# Revit family: 879-006X99-001-DN65-600
name_source: partatom
category: Pipe Accessories
units: mm (PartAtom-declared; Revit-internal decimal feet)

## family parameters
Always vertical = Yes
Cut with Voids When Loaded = No
Part Type = Valve - Breaks Into
Round Connector Dimension = Use Diameter
Shared = No
Work Plane-Based = No

## types (49) — shared parameters
879-0065-00-14400609999 = DN65_PN10/16
879-0065-00-14400619999 = DN65_PN10/16
879-0065-00-14400629999 = DN65_PN10/16
879-0065-00-144006299A0 = DN65_PN10/16
879-0080-00-14400609999 = DN80_PN10/16
879-0080-00-14400619999 = DN80_PN10/16
879-0080-00-14400629999 = DN80_PN10/16
879-0080-00-144006299A0 = DN80_PN10/16
879-0100-00-14400609999 = DN100_PN10/16
879-0100-00-14400619999 = DN100_PN10/16
879-0100-00-14400629999 = DN100_PN10/16
879-0100-00-144006299A0 = DN100_PN10/16
879-0125-00-14400609999 = DN125_PN10/16
879-0125-00-14400619999 = DN125_PN10/16
879-0125-00-14400629999 = DN125_PN10/16
879-0125-00-144006299A0 = DN125_PN10/16
879-0150-00-14400609999 = DN150_PN10/16
879-0150-00-14400619999 = DN150_PN10/16
879-0150-00-14400629999 = DN150_PN10/16
879-0150-00-144006299A0 = DN150_PN10/16
879-0200-00-04400609999 = DN200_PN10
879-0200-00-04400619999 = DN200_PN10
879-0200-00-04400629999 = DN200_PN10
879-0200-00-14400609999 = DN200_PN16
879-0200-00-14400619999 = DN200_PN16
879-0200-00-14400629999 = DN200_PN16
879-0200-00-144006299A0 = DN200_PN16
879-0250-00-04400609999 = DN250_PN10
879-0250-00-04400619999 = DN250_PN10
879-0250-00-04400629999 = DN250_PN10
879-0250-00-14400609999 = DN250_PN16
879-0250-00-14400619999 = DN250_PN16
879-0250-00-14400629999 = DN250_PN16
879-0250-00-144006299A0 = DN250_PN16
879-0300-00-04400609999 = DN300_PN10
879-0300-00-04400619999 = DN300_PN10
879-0300-00-04400629999 = DN300_PN10
879-0300-00-14400609999 = DN300_PN16
879-0300-00-14400619999 = DN300_PN16
879-0300-00-14400629999 = DN300_PN16
879-0300-00-144006299A0 = DN300_PN16
879-0350-00-04400609999 = DN350_PN10
879-0350-00-04400619999 = DN350_PN10
879-0350-00-04400629999 = DN350_PN10
879-0350-00-144006299A0 = DN350_PN16
879-0400-00-144006299A0 = DN400_PN16
879-0450-00-144006299A0 = DN450_PN16
879-0500-00-144006299A0 = DN500_PN16
879-0600-00-144006299A0 = DN600_PN16
Body_wall_thickness = 10 mm  [stored 0.0328084 ft]
Description_ = AVK ON/OFF FLOAT LEVEL CONTROL VALVE
Search_Table = 879-006X99-001-DN65-600
URL product pages = https://www.avkvalves.com

## per-type parameters (varying)
- 879-0065-00-14400609999_DN65_PN10/16: Body_Collar_Dia=30 mm  [stored 0.0984252 ft]; Body_Collar_Dia_2=21 mm  [stored 0.0688976 ft]; Body_Flange_Dia=94 mm; Body_Flange_Dia_2=104 mm; Body_Height_1=64 mm; Body_Height_2=36 mm  [stored 0.11811 ft]; Body_Height_3=45 mm; Body_Height_4=51 mm; Body_Top_Dia=13 mm; Body_Top_Dia_2=11 mm; Body_With_Dia=36 mm  [stored 0.11811 ft]; Body_With_Dia_1=73 mm; Body_With_Dia_2=78 mm; Bolt_support=223 mm; Bolt_support_2=112 mm; Bolt_support_Dia=12 mm  [stored 0.0393701 ft]; Bolt_support_lenght=53 mm; Bolt_support_lenght_2=63 mm; Bottom_profile=16 mm  [stored 0.0524934 ft]; D1=59 mm; D3=93 mm; DN=65 mm; Fillet_Length=6 mm  [stored 0.019685 ft]; Fillet_Length_Ref=18 mm  [stored 0.0590551 ft]; Flange_thickness=19 mm  [stored 0.062336 ft]; H=290 mm; H3_Ref=284 mm; ID=33 mm; L=290 mm; PG_Dia=33 mm; PG_Ref=43 mm  [stored 0.141076 ft]; PG_depth=8 mm  [stored 0.0262467 ft]; PG_height=198 mm; PG_height_1=182 mm; PG_ref=43 mm  [stored 0.141076 ft]; P_lenght=39 mm  [stored 0.127953 ft]; Pilot_Dia_1=18 mm  [stored 0.0590551 ft]; Pilot_Dia_2=35 mm  [stored 0.114829 ft]; Pilot_Dia_3=12 mm  [stored 0.0393701 ft]; Pilot_Dia_4=6 mm  [stored 0.019685 ft]; Pilot_Dia_5=4 mm  [stored 0.0131234 ft]; Pilot_top_1=187 mm; Profile1_Height=117 mm; Profile1_Length=25 mm  [stored 0.082021 ft]; Profile1_Length_2=17 mm; Profile_Dia=6 mm  [stored 0.019685 ft]; Profile_Dia_2=6 mm  [stored 0.019685 ft]; Profile_Dia_3=12 mm  [stored 0.0393701 ft]; Profile_height ref=41 mm  [stored 0.134514 ft]; Top_Profile=134 mm; Top_Profile_Ref=139 mm; W=259 mm; W_Ref=253 mm
- 879-0065-00-14400619999_DN65_PN10/16: Body_Collar_Dia=30 mm  [stored 0.0984252 ft]; Body_Collar_Dia_2=21 mm  [stored 0.0688976 ft]; Body_Flange_Dia=94 mm; Body_Flange_Dia_2=104 mm; Body_Height_1=64 mm; Body_Height_2=36 mm  [stored 0.11811 ft]; Body_Height_3=45 mm; Body_Height_4=51 mm; Body_Top_Dia=13 mm; Body_Top_Dia_2=11 mm; Body_With_Dia=36 mm  [stored 0.11811 ft]; Body_With_Dia_1=73 mm; Body_With_Dia_2=78 mm; Bolt_support=223 mm; Bolt_support_2=112 mm; Bolt_support_Dia=12 mm  [stored 0.0393701 ft]; Bolt_support_lenght=53 mm; Bolt_support_lenght_2=63 mm; Bottom_profile=16 mm  [stored 0.0524934 ft]; D1=59 mm; D3=93 mm; DN=65 mm; Fillet_Length=6 mm  [stored 0.019685 ft]; Fillet_Length_Ref=18 mm  [stored 0.0590551 ft]; Flange_thickness=19 mm  [stored 0.062336 ft]; H=290 mm; H3_Ref=284 mm; ID=33 mm; L=290 mm; PG_Dia=33 mm; PG_Ref=43 mm  [stored 0.141076 ft]; PG_depth=8 mm  [stored 0.0262467 ft]; PG_height=212 mm; PG_height_1=196 mm; PG_ref=43 mm  [stored 0.141076 ft]; P_lenght=39 mm  [stored 0.127953 ft]; Pilot_Dia_1=18 mm  [stored 0.0590551 ft]; Pilot_Dia_2=35 mm  [stored 0.114829 ft]; Pilot_Dia_3=12 mm  [stored 0.0393701 ft]; Pilot_Dia_4=6 mm  [stored 0.019685 ft]; Pilot_Dia_5=4 mm  [stored 0.0131234 ft]; Pilot_top_1=187 mm; Profile1_Height=135 mm; Profile1_Length=25 mm  [stored 0.082021 ft]; Profile1_Length_2=17 mm; Profile_Dia=6 mm  [stored 0.019685 ft]; Profile_Dia_2=6 mm  [stored 0.019685 ft]; Profile_Dia_3=12 mm  [stored 0.0393701 ft]; Profile_height ref=41 mm  [stored 0.134514 ft]; Top_Profile=134 mm; Top_Profile_Ref=139 mm; W=259 mm; W_Ref=253 mm
- 879-0065-00-14400629999_DN65_PN10/16: Body_Collar_Dia=30 mm  [stored 0.0984252 ft]; Body_Collar_Dia_2=21 mm  [stored 0.0688976 ft]; Body_Flange_Dia=94 mm; Body_Flange_Dia_2=104 mm; Body_Height_1=64 mm; Body_Height_2=36 mm  [stored 0.11811 ft]; Body_Height_3=45 mm; Body_Height_4=51 mm; Body_Top_Dia=13 mm; Body_Top_Dia_2=11 mm; Body_With_Dia=36 mm  [stored 0.11811 ft]; Body_With_Dia_1=73 mm; Body_With_Dia_2=78 mm; Bolt_support=223 mm; Bolt_support_2=112 mm; Bolt_support_Dia=12 mm  [stored 0.0393701 ft]; Bolt_support_lenght=53 mm; Bolt_support_lenght_2=63 mm; Bottom_profile=16 mm  [stored 0.0524934 ft]; D1=59 mm; D3=93 mm; DN=65 mm; Fillet_Length=6 mm  [stored 0.019685 ft]; Fillet_Length_Ref=18 mm  [stored 0.0590551 ft]; Flange_thickness=19 mm  [stored 0.062336 ft]; H=290 mm; H3_Ref=284 mm; ID=33 mm; L=290 mm; PG_Dia=33 mm; PG_Ref=43 mm  [stored 0.141076 ft]; PG_depth=8 mm  [stored 0.0262467 ft]; PG_height=198 mm; PG_height_1=182 mm; PG_ref=43 mm  [stored 0.141076 ft]; P_lenght=39 mm  [stored 0.127953 ft]; Pilot_Dia_1=18 mm  [stored 0.0590551 ft]; Pilot_Dia_2=35 mm  [stored 0.114829 ft]; Pilot_Dia_3=12 mm  [stored 0.0393701 ft]; Pilot_Dia_4=6 mm  [stored 0.019685 ft]; Pilot_Dia_5=4 mm  [stored 0.0131234 ft]; Pilot_top_1=187 mm; Profile1_Height=117 mm; Profile1_Length=25 mm  [stored 0.082021 ft]; Profile1_Length_2=17 mm; Profile_Dia=6 mm  [stored 0.019685 ft]; Profile_Dia_2=6 mm  [stored 0.019685 ft]; Profile_Dia_3=12 mm  [stored 0.0393701 ft]; Profile_height ref=41 mm  [stored 0.134514 ft]; Top_Profile=134 mm; Top_Profile_Ref=139 mm; W=259 mm; W_Ref=253 mm
- 879-0065-00-144006299A0_DN65_PN10/16: Body_Collar_Dia=30 mm  [stored 0.0984252 ft]; Body_Collar_Dia_2=21 mm  [stored 0.0688976 ft]; Body_Flange_Dia=94 mm; Body_Flange_Dia_2=104 mm; Body_Height_1=64 mm; Body_Height_2=36 mm  [stored 0.11811 ft]; Body_Height_3=73 mm; Body_Height_4=51 mm; Body_Top_Dia=13 mm; Body_Top_Dia_2=11 mm; Body_With_Dia=36 mm  [stored 0.11811 ft]; Body_With_Dia_1=73 mm; Body_With_Dia_2=78 mm; Bolt_support=223 mm; Bolt_support_2=112 mm; Bolt_support_Dia=12 mm  [stored 0.0393701 ft]; Bolt_support_lenght=53 mm; Bolt_support_lenght_2=63 mm; Bottom_profile=16 mm  [stored 0.0524934 ft]; D1=59 mm; D3=93 mm; DN=65 mm; Fillet_Length=6 mm  [stored 0.019685 ft]; Fillet_Length_Ref=18 mm  [stored 0.0590551 ft]; Flange_thickness=19 mm  [stored 0.062336 ft]; H=424 mm; H3_Ref=418 mm; ID=33 mm; L=290 mm; PG_Dia=33 mm; PG_Ref=43 mm  [stored 0.141076 ft]; PG_depth=8 mm  [stored 0.0262467 ft]; PG_height=242 mm; PG_height_1=226 mm; PG_ref=43 mm  [stored 0.141076 ft]; P_lenght=39 mm  [stored 0.127953 ft]; Pilot_Dia_1=18 mm  [stored 0.0590551 ft]; Pilot_Dia_2=35 mm  [stored 0.114829 ft]; Pilot_Dia_3=12 mm  [stored 0.0393701 ft]; Pilot_Dia_4=6 mm  [stored 0.019685 ft]; Pilot_Dia_5=4 mm  [stored 0.0131234 ft]; Pilot_top_1=261 mm; Profile1_Height=135 mm; Profile1_Length=25 mm  [stored 0.082021 ft]; Profile1_Length_2=17 mm; Profile_Dia=6 mm  [stored 0.019685 ft]; Profile_Dia_2=6 mm  [stored 0.019685 ft]; Profile_Dia_3=12 mm  [stored 0.0393701 ft]; Profile_height ref=41 mm  [stored 0.134514 ft]; Top_Profile=134 mm; Top_Profile_Ref=139 mm; W=259 mm; W_Ref=253 mm
- 879-0080-00-14400609999_DN80_PN10/16: Body_Collar_Dia=32 mm; Body_Collar_Dia_2=22 mm  [stored 0.0721785 ft]; Body_Flange_Dia=100 mm; Body_Flange_Dia_2=111 mm; Body_Height_1=69 mm; Body_Height_2=39 mm  [stored 0.127953 ft]; Body_Height_3=50 mm; Body_Height_4=54 mm; Body_Top_Dia=14 mm  [stored 0.0459318 ft]; Body_Top_Dia_2=12 mm  [stored 0.0393701 ft]; Body_With_Dia=39 mm  [stored 0.127953 ft]; Body_With_Dia_1=78 mm; Body_With_Dia_2=84 mm; Bolt_support=238 mm; Bolt_support_2=119 mm; Bolt_support_Dia=12 mm  [stored 0.0393701 ft]; Bolt_support_lenght=60 mm; Bolt_support_lenght_2=70 mm; Bottom_profile=20 mm  [stored 0.0656168 ft]; D1=66 mm; D3=100 mm; DN=80 mm; Fillet_Length=6 mm  [stored 0.019685 ft]; Fillet_Length_Ref=18 mm  [stored 0.0590551 ft]; Flange_thickness=19 mm  [stored 0.062336 ft]; H=307 mm; H3_Ref=301 mm; ID=40 mm  [stored 0.131234 ft]; L=310 mm; PG_Dia=40 mm  [stored 0.131234 ft]; PG_Ref=46 mm; PG_depth=8 mm  [stored 0.0262467 ft]; PG_height=229 mm; PG_height_1=209 mm; PG_ref=50 mm; P_lenght=43 mm  [stored 0.141076 ft]; Pilot_Dia_1=20 mm  [stored 0.0656168 ft]; Pilot_Dia_2=39 mm  [stored 0.127953 ft]; Pilot_Dia_3=13 mm; Pilot_Dia_4=7 mm  [stored 0.0229659 ft]; Pilot_Dia_5=4 mm  [stored 0.0131234 ft]; Pilot_top_1=197 mm; Profile1_Height=144 mm; Profile1_Length=27 mm; Profile1_Length_2=18 mm  [stored 0.0590551 ft]; Profile_Dia=6 mm  [stored 0.019685 ft]; Profile_Dia_2=6 mm  [stored 0.019685 ft]; Profile_Dia_3=12 mm  [stored 0.0393701 ft]; Profile_height ref=41 mm  [stored 0.134514 ft]; Top_Profile=143 mm; Top_Profile_Ref=148 mm; W=281 mm; W_Ref=275 mm
- 879-0080-00-14400619999_DN80_PN10/16: Body_Collar_Dia=32 mm; Body_Collar_Dia_2=22 mm  [stored 0.0721785 ft]; Body_Flange_Dia=100 mm; Body_Flange_Dia_2=111 mm; Body_Height_1=69 mm; Body_Height_2=39 mm  [stored 0.127953 ft]; Body_Height_3=50 mm; Body_Height_4=54 mm; Body_Top_Dia=14 mm  [stored 0.0459318 ft]; Body_Top_Dia_2=12 mm  [stored 0.0393701 ft]; Body_With_Dia=39 mm  [stored 0.127953 ft]; Body_With_Dia_1=78 mm; Body_With_Dia_2=84 mm; Bolt_support=238 mm; Bolt_support_2=119 mm; Bolt_support_Dia=12 mm  [stored 0.0393701 ft]; Bolt_support_lenght=60 mm; Bolt_support_lenght_2=70 mm; Bottom_profile=20 mm  [stored 0.0656168 ft]; D1=66 mm; D3=100 mm; DN=80 mm; Fillet_Length=6 mm  [stored 0.019685 ft]; Fillet_Length_Ref=18 mm  [stored 0.0590551 ft]; Flange_thickness=19 mm  [stored 0.062336 ft]; H=307 mm; H3_Ref=301 mm; ID=40 mm  [stored 0.131234 ft]; L=310 mm; PG_Dia=40 mm  [stored 0.131234 ft]; PG_Ref=46 mm; PG_depth=8 mm  [stored 0.0262467 ft]; PG_height=220 mm; PG_height_1=200 mm; PG_ref=50 mm; P_lenght=43 mm  [stored 0.141076 ft]; Pilot_Dia_1=20 mm  [stored 0.0656168 ft]; Pilot_Dia_2=39 mm  [stored 0.127953 ft]; Pilot_Dia_3=13 mm; Pilot_Dia_4=7 mm  [stored 0.0229659 ft]; Pilot_Dia_5=4 mm  [stored 0.0131234 ft]; Pilot_top_1=197 mm; Profile1_Height=133 mm; Profile1_Length=27 mm; Profile1_Length_2=18 mm  [stored 0.0590551 ft]; Profile_Dia=6 mm  [stored 0.019685 ft]; Profile_Dia_2=6 mm  [stored 0.019685 ft]; Profile_Dia_3=12 mm  [stored 0.0393701 ft]; Profile_height ref=41 mm  [stored 0.134514 ft]; Top_Profile=143 mm; Top_Profile_Ref=148 mm; W=281 mm; W_Ref=275 mm
- 879-0080-00-14400629999_DN80_PN10/16: Body_Collar_Dia=32 mm; Body_Collar_Dia_2=22 mm  [stored 0.0721785 ft]; Body_Flange_Dia=100 mm; Body_Flange_Dia_2=111 mm; Body_Height_1=69 mm; Body_Height_2=39 mm  [stored 0.127953 ft]; Body_Height_3=50 mm; Body_Height_4=54 mm; Body_Top_Dia=14 mm  [stored 0.0459318 ft]; Body_Top_Dia_2=12 mm  [stored 0.0393701 ft]; Body_With_Dia=39 mm  [stored 0.127953 ft]; Body_With_Dia_1=78 mm; Body_With_Dia_2=84 mm; Bolt_support=238 mm; Bolt_support_2=119 mm; Bolt_support_Dia=12 mm  [stored 0.0393701 ft]; Bolt_support_lenght=60 mm; Bolt_support_lenght_2=70 mm; Bottom_profile=20 mm  [stored 0.0656168 ft]; D1=66 mm; D3=100 mm; DN=80 mm; Fillet_Length=6 mm  [stored 0.019685 ft]; Fillet_Length_Ref=18 mm  [stored 0.0590551 ft]; Flange_thickness=19 mm  [stored 0.062336 ft]; H=307 mm; H3_Ref=301 mm; ID=40 mm  [stored 0.131234 ft]; L=310 mm; PG_Dia=40 mm  [stored 0.131234 ft]; PG_Ref=46 mm; PG_depth=8 mm  [stored 0.0262467 ft]; PG_height=229 mm; PG_height_1=209 mm; PG_ref=50 mm; P_lenght=43 mm  [stored 0.141076 ft]; Pilot_Dia_1=20 mm  [stored 0.0656168 ft]; Pilot_Dia_2=39 mm  [stored 0.127953 ft]; Pilot_Dia_3=13 mm; Pilot_Dia_4=7 mm  [stored 0.0229659 ft]; Pilot_Dia_5=4 mm  [stored 0.0131234 ft]; Pilot_top_1=197 mm; Profile1_Height=144 mm; Profile1_Length=27 mm; Profile1_Length_2=18 mm  [stored 0.0590551 ft]; Profile_Dia=6 mm  [stored 0.019685 ft]; Profile_Dia_2=6 mm  [stored 0.019685 ft]; Profile_Dia_3=12 mm  [stored 0.0393701 ft]; Profile_height ref=41 mm  [stored 0.134514 ft]; Top_Profile=143 mm; Top_Profile_Ref=148 mm; W=281 mm; W_Ref=275 mm
- 879-0080-00-144006299A0_DN80_PN10/16: Body_Collar_Dia=32 mm; Body_Collar_Dia_2=22 mm  [stored 0.0721785 ft]; Body_Flange_Dia=100 mm; Body_Flange_Dia_2=111 mm; Body_Height_1=69 mm; Body_Height_2=39 mm  [stored 0.127953 ft]; Body_Height_3=78 mm; Body_Height_4=54 mm; Body_Top_Dia=14 mm  [stored 0.0459318 ft]; Body_Top_Dia_2=12 mm  [stored 0.0393701 ft]; Body_With_Dia=39 mm  [stored 0.127953 ft]; Body_With_Dia_1=78 mm; Body_With_Dia_2=84 mm; Bolt_support=238 mm; Bolt_support_2=119 mm; Bolt_support_Dia=12 mm  [stored 0.0393701 ft]; Bolt_support_lenght=60 mm; Bolt_support_lenght_2=70 mm; Bottom_profile=20 mm  [stored 0.0656168 ft]; D1=66 mm; D3=100 mm; DN=80 mm; Fillet_Length=6 mm  [stored 0.019685 ft]; Fillet_Length_Ref=18 mm  [stored 0.0590551 ft]; Flange_thickness=19 mm  [stored 0.062336 ft]; H=447 mm; H3_Ref=441 mm; ID=40 mm  [stored 0.131234 ft]; L=310 mm; PG_Dia=40 mm  [stored 0.131234 ft]; PG_Ref=46 mm; PG_depth=8 mm  [stored 0.0262467 ft]; PG_height=252 mm; PG_height_1=232 mm; PG_ref=50 mm; P_lenght=43 mm  [stored 0.141076 ft]; Pilot_Dia_1=20 mm  [stored 0.0656168 ft]; Pilot_Dia_2=39 mm  [stored 0.127953 ft]; Pilot_Dia_3=13 mm; Pilot_Dia_4=7 mm  [stored 0.0229659 ft]; Pilot_Dia_5=4 mm  [stored 0.0131234 ft]; Pilot_top_1=275 mm; Profile1_Height=133 mm; Profile1_Length=27 mm; Profile1_Length_2=18 mm  [stored 0.0590551 ft]; Profile_Dia=6 mm  [stored 0.019685 ft]; Profile_Dia_2=6 mm  [stored 0.019685 ft]; Profile_Dia_3=12 mm  [stored 0.0393701 ft]; Profile_height ref=41 mm  [stored 0.134514 ft]; Top_Profile=143 mm; Top_Profile_Ref=148 mm; W=281 mm; W_Ref=275 mm
- 879-0100-00-14400609999_DN100_PN10/16: Body_Collar_Dia=36 mm  [stored 0.11811 ft]; Body_Collar_Dia_2=25 mm  [stored 0.082021 ft]; Body_Flange_Dia=113 mm; Body_Flange_Dia_2=125 mm; Body_Height_1=78 mm; Body_Height_2=44 mm; Body_Height_3=40 mm  [stored 0.131234 ft]; Body_Height_4=59 mm; Body_Top_Dia=16 mm  [stored 0.0524934 ft]; Body_Top_Dia_2=13 mm; Body_With_Dia=44 mm; Body_With_Dia_1=88 mm; Body_With_Dia_2=95 mm; Bolt_support=269 mm; Bolt_support_2=135 mm; Bolt_support_Dia=12 mm  [stored 0.0393701 ft]; Bolt_support_lenght=70 mm; Bolt_support_lenght_2=80 mm; Bottom_profile=25 mm  [stored 0.082021 ft]; D1=78 mm; D3=110 mm; DN=100 mm; Fillet_Length=6 mm  [stored 0.019685 ft]; Fillet_Length_Ref=18 mm  [stored 0.0590551 ft]; Flange_thickness=19 mm  [stored 0.062336 ft]; H=322 mm; H3_Ref=316 mm; ID=50 mm; L=350 mm; PG_Dia=50 mm; PG_Ref=52 mm; PG_depth=8 mm  [stored 0.0262467 ft]; PG_height=244 mm; PG_height_1=219 mm; PG_ref=60 mm; P_lenght=48 mm; Pilot_Dia_1=22 mm  [stored 0.0721785 ft]; Pilot_Dia_2=44 mm; Pilot_Dia_3=15 mm  [stored 0.0492126 ft]; Pilot_Dia_4=7 mm  [stored 0.0229659 ft]; Pilot_Dia_5=5 mm  [stored 0.0164042 ft]; Pilot_top_1=205 mm; Profile1_Height=150 mm; Profile1_Length=30 mm  [stored 0.0984252 ft]; Profile1_Length_2=20 mm  [stored 0.0656168 ft]; Profile_Dia=6 mm  [stored 0.019685 ft]; Profile_Dia_2=6 mm  [stored 0.019685 ft]; Profile_Dia_3=12 mm  [stored 0.0393701 ft]; Profile_height ref=41 mm  [stored 0.134514 ft]; Top_Profile=162 mm; Top_Profile_Ref=167 mm; W=300 mm; W_Ref=294 mm
- 879-0100-00-14400619999_DN100_PN10/16: Body_Collar_Dia=36 mm  [stored 0.11811 ft]; Body_Collar_Dia_2=25 mm  [stored 0.082021 ft]; Body_Flange_Dia=113 mm; Body_Flange_Dia_2=125 mm; Body_Height_1=78 mm; Body_Height_2=44 mm; Body_Height_3=40 mm  [stored 0.131234 ft]; Body_Height_4=59 mm; Body_Top_Dia=16 mm  [stored 0.0524934 ft]; Body_Top_Dia_2=13 mm; Body_With_Dia=44 mm; Body_With_Dia_1=88 mm; Body_With_Dia_2=95 mm; Bolt_support=269 mm; Bolt_support_2=135 mm; Bolt_support_Dia=12 mm  [stored 0.0393701 ft]; Bolt_support_lenght=70 mm; Bolt_support_lenght_2=80 mm; Bottom_profile=25 mm  [stored 0.082021 ft]; D1=78 mm; D3=110 mm; DN=100 mm; Fillet_Length=6 mm  [stored 0.019685 ft]; Fillet_Length_Ref=18 mm  [stored 0.0590551 ft]; Flange_thickness=19 mm  [stored 0.062336 ft]; H=322 mm; H3_Ref=316 mm; ID=50 mm; L=350 mm; PG_Dia=50 mm; PG_Ref=52 mm; PG_depth=8 mm  [stored 0.0262467 ft]; PG_height=237 mm; PG_height_1=212 mm; PG_ref=60 mm; P_lenght=48 mm; Pilot_Dia_1=22 mm  [stored 0.0721785 ft]; Pilot_Dia_2=44 mm; Pilot_Dia_3=15 mm  [stored 0.0492126 ft]; Pilot_Dia_4=7 mm  [stored 0.0229659 ft]; Pilot_Dia_5=5 mm  [stored 0.0164042 ft]; Pilot_top_1=205 mm; Profile1_Height=141 mm; Profile1_Length=30 mm  [stored 0.0984252 ft]; Profile1_Length_2=20 mm  [stored 0.0656168 ft]; Profile_Dia=6 mm  [stored 0.019685 ft]; Profile_Dia_2=6 mm  [stored 0.019685 ft]; Profile_Dia_3=12 mm  [stored 0.0393701 ft]; Profile_height ref=41 mm  [stored 0.134514 ft]; Top_Profile=162 mm; Top_Profile_Ref=167 mm; W=300 mm; W_Ref=294 mm
- 879-0100-00-14400629999_DN100_PN10/16: Body_Collar_Dia=36 mm  [stored 0.11811 ft]; Body_Collar_Dia_2=25 mm  [stored 0.082021 ft]; Body_Flange_Dia=113 mm; Body_Flange_Dia_2=125 mm; Body_Height_1=78 mm; Body_Height_2=44 mm; Body_Height_3=40 mm  [stored 0.131234 ft]; Body_Height_4=59 mm; Body_Top_Dia=16 mm  [stored 0.0524934 ft]; Body_Top_Dia_2=13 mm; Body_With_Dia=44 mm; Body_With_Dia_1=88 mm; Body_With_Dia_2=95 mm; Bolt_support=269 mm; Bolt_support_2=135 mm; Bolt_support_Dia=12 mm  [stored 0.0393701 ft]; Bolt_support_lenght=70 mm; Bolt_support_lenght_2=80 mm; Bottom_profile=25 mm  [stored 0.082021 ft]; D1=78 mm; D3=110 mm; DN=100 mm; Fillet_Length=6 mm  [stored 0.019685 ft]; Fillet_Length_Ref=18 mm  [stored 0.0590551 ft]; Flange_thickness=19 mm  [stored 0.062336 ft]; H=322 mm; H3_Ref=316 mm; ID=50 mm; L=350 mm; PG_Dia=50 mm; PG_Ref=52 mm; PG_depth=8 mm  [stored 0.0262467 ft]; PG_height=244 mm; PG_height_1=219 mm; PG_ref=60 mm; P_lenght=48 mm; Pilot_Dia_1=22 mm  [stored 0.0721785 ft]; Pilot_Dia_2=44 mm; Pilot_Dia_3=15 mm  [stored 0.0492126 ft]; Pilot_Dia_4=7 mm  [stored 0.0229659 ft]; Pilot_Dia_5=5 mm  [stored 0.0164042 ft]; Pilot_top_1=205 mm; Profile1_Height=150 mm; Profile1_Length=30 mm  [stored 0.0984252 ft]; Profile1_Length_2=20 mm  [stored 0.0656168 ft]; Profile_Dia=6 mm  [stored 0.019685 ft]; Profile_Dia_2=6 mm  [stored 0.019685 ft]; Profile_Dia_3=12 mm  [stored 0.0393701 ft]; Profile_height ref=41 mm  [stored 0.134514 ft]; Top_Profile=162 mm; Top_Profile_Ref=167 mm; W=300 mm; W_Ref=294 mm
- 879-0100-00-144006299A0_DN100_PN10/16: Body_Collar_Dia=36 mm  [stored 0.11811 ft]; Body_Collar_Dia_2=25 mm  [stored 0.082021 ft]; Body_Flange_Dia=113 mm; Body_Flange_Dia_2=125 mm; Body_Height_1=78 mm; Body_Height_2=44 mm; Body_Height_3=70 mm; Body_Height_4=59 mm; Body_Top_Dia=16 mm  [stored 0.0524934 ft]; Body_Top_Dia_2=13 mm; Body_With_Dia=44 mm; Body_With_Dia_1=88 mm; Body_With_Dia_2=95 mm; Bolt_support=269 mm; Bolt_support_2=135 mm; Bolt_support_Dia=12 mm  [stored 0.0393701 ft]; Bolt_support_lenght=70 mm; Bolt_support_lenght_2=80 mm; Bottom_profile=25 mm  [stored 0.082021 ft]; D1=78 mm; D3=110 mm; DN=100 mm; Fillet_Length=6 mm  [stored 0.019685 ft]; Fillet_Length_Ref=18 mm  [stored 0.0590551 ft]; Flange_thickness=19 mm  [stored 0.062336 ft]; H=461 mm; H3_Ref=455 mm; ID=50 mm; L=350 mm; PG_Dia=50 mm; PG_Ref=52 mm; PG_depth=8 mm  [stored 0.0262467 ft]; PG_height=269 mm; PG_height_1=244 mm; PG_ref=60 mm; P_lenght=48 mm; Pilot_Dia_1=22 mm  [stored 0.0721785 ft]; Pilot_Dia_2=44 mm; Pilot_Dia_3=15 mm  [stored 0.0492126 ft]; Pilot_Dia_4=7 mm  [stored 0.0229659 ft]; Pilot_Dia_5=5 mm  [stored 0.0164042 ft]; Pilot_top_1=281 mm; Profile1_Height=141 mm; Profile1_Length=30 mm  [stored 0.0984252 ft]; Profile1_Length_2=20 mm  [stored 0.0656168 ft]; Profile_Dia=6 mm  [stored 0.019685 ft]; Profile_Dia_2=6 mm  [stored 0.019685 ft]; Profile_Dia_3=12 mm  [stored 0.0393701 ft]; Profile_height ref=41 mm  [stored 0.134514 ft]; Top_Profile=162 mm; Top_Profile_Ref=167 mm; W=300 mm; W_Ref=294 mm
- 879-0125-00-14400609999_DN125_PN10/16: Body_Collar_Dia=42 mm  [stored 0.137795 ft]; Body_Collar_Dia_2=29 mm; Body_Flange_Dia=129 mm; Body_Flange_Dia_2=143 mm; Body_Height_1=89 mm; Body_Height_2=50 mm; Body_Height_3=35 mm  [stored 0.114829 ft]; Body_Height_4=65 mm; Body_Top_Dia=18 mm  [stored 0.0590551 ft]; Body_Top_Dia_2=15 mm  [stored 0.0492126 ft]; Body_With_Dia=50 mm; Body_With_Dia_1=100 mm; Body_With_Dia_2=108 mm; Bolt_support=308 mm; Bolt_support_2=154 mm; Bolt_support_Dia=12 mm  [stored 0.0393701 ft]; Bolt_support_lenght=83 mm; Bolt_support_lenght_2=93 mm; Bottom_profile=31 mm  [stored 0.101706 ft]; D1=92 mm; D3=125 mm; DN=125 mm; Fillet_Length=6 mm  [stored 0.019685 ft]; Fillet_Length_Ref=18 mm  [stored 0.0590551 ft]; Flange_thickness=19 mm  [stored 0.062336 ft]; H=341 mm; H3_Ref=335 mm; ID=63 mm; L=400 mm; PG_Dia=63 mm; PG_Ref=59 mm; PG_depth=8 mm  [stored 0.0262467 ft]; PG_height=273 mm; PG_height_1=242 mm; PG_ref=73 mm; P_lenght=61 mm; Pilot_Dia_1=28 mm  [stored 0.0918635 ft]; Pilot_Dia_2=55 mm; Pilot_Dia_3=18 mm  [stored 0.0590551 ft]; Pilot_Dia_4=9 mm  [stored 0.0295276 ft]; Pilot_Dia_5=6 mm  [stored 0.019685 ft]; Pilot_top_1=217 mm; Profile1_Height=170 mm; Profile1_Length=34 mm; Profile1_Length_2=23 mm  [stored 0.0754593 ft]; Profile_Dia=6 mm  [stored 0.019685 ft]; Profile_Dia_2=6 mm  [stored 0.019685 ft]; Profile_Dia_3=12 mm  [stored 0.0393701 ft]; Profile_height ref=41 mm  [stored 0.134514 ft]; Top_Profile=185 mm; Top_Profile_Ref=190 mm; W=320 mm; W_Ref=314 mm
- 879-0125-00-14400619999_DN125_PN10/16: Body_Collar_Dia=42 mm  [stored 0.137795 ft]; Body_Collar_Dia_2=29 mm; Body_Flange_Dia=129 mm; Body_Flange_Dia_2=143 mm; Body_Height_1=89 mm; Body_Height_2=50 mm; Body_Height_3=35 mm  [stored 0.114829 ft]; Body_Height_4=65 mm; Body_Top_Dia=18 mm  [stored 0.0590551 ft]; Body_Top_Dia_2=15 mm  [stored 0.0492126 ft]; Body_With_Dia=50 mm; Body_With_Dia_1=100 mm; Body_With_Dia_2=108 mm; Bolt_support=308 mm; Bolt_support_2=154 mm; Bolt_support_Dia=12 mm  [stored 0.0393701 ft]; Bolt_support_lenght=83 mm; Bolt_support_lenght_2=93 mm; Bottom_profile=31 mm  [stored 0.101706 ft]; D1=92 mm; D3=125 mm; DN=125 mm; Fillet_Length=6 mm  [stored 0.019685 ft]; Fillet_Length_Ref=18 mm  [stored 0.0590551 ft]; Flange_thickness=19 mm  [stored 0.062336 ft]; H=341 mm; H3_Ref=335 mm; ID=63 mm; L=400 mm; PG_Dia=63 mm; PG_Ref=59 mm; PG_depth=8 mm  [stored 0.0262467 ft]; PG_height=266 mm; PG_height_1=234 mm; PG_ref=73 mm; P_lenght=61 mm; Pilot_Dia_1=28 mm  [stored 0.0918635 ft]; Pilot_Dia_2=55 mm; Pilot_Dia_3=18 mm  [stored 0.0590551 ft]; Pilot_Dia_4=9 mm  [stored 0.0295276 ft]; Pilot_Dia_5=6 mm  [stored 0.019685 ft]; Pilot_top_1=223 mm; Profile1_Height=160 mm; Profile1_Length=34 mm; Profile1_Length_2=23 mm  [stored 0.0754593 ft]; Profile_Dia=6 mm  [stored 0.019685 ft]; Profile_Dia_2=6 mm  [stored 0.019685 ft]; Profile_Dia_3=12 mm  [stored 0.0393701 ft]; Profile_height ref=41 mm  [stored 0.134514 ft]; Top_Profile=185 mm; Top_Profile_Ref=190 mm; W=320 mm; W_Ref=314 mm
- 879-0125-00-14400629999_DN125_PN10/16: Body_Collar_Dia=42 mm  [stored 0.137795 ft]; Body_Collar_Dia_2=29 mm; Body_Flange_Dia=129 mm; Body_Flange_Dia_2=143 mm; Body_Height_1=89 mm; Body_Height_2=50 mm; Body_Height_3=35 mm  [stored 0.114829 ft]; Body_Height_4=65 mm; Body_Top_Dia=18 mm  [stored 0.0590551 ft]; Body_Top_Dia_2=15 mm  [stored 0.0492126 ft]; Body_With_Dia=50 mm; Body_With_Dia_1=100 mm; Body_With_Dia_2=108 mm; Bolt_support=308 mm; Bolt_support_2=154 mm; Bolt_support_Dia=12 mm  [stored 0.0393701 ft]; Bolt_support_lenght=83 mm; Bolt_support_lenght_2=93 mm; Bottom_profile=31 mm  [stored 0.101706 ft]; D1=92 mm; D3=125 mm; DN=125 mm; Fillet_Length=6 mm  [stored 0.019685 ft]; Fillet_Length_Ref=18 mm  [stored 0.0590551 ft]; Flange_thickness=19 mm  [stored 0.062336 ft]; H=341 mm; H3_Ref=335 mm; ID=63 mm; L=400 mm; PG_Dia=63 mm; PG_Ref=59 mm; PG_depth=8 mm  [stored 0.0262467 ft]; PG_height=273 mm; PG_height_1=242 mm; PG_ref=73 mm; P_lenght=61 mm; Pilot_Dia_1=28 mm  [stored 0.0918635 ft]; Pilot_Dia_2=55 mm; Pilot_Dia_3=18 mm  [stored 0.0590551 ft]; Pilot_Dia_4=9 mm  [stored 0.0295276 ft]; Pilot_Dia_5=6 mm  [stored 0.019685 ft]; Pilot_top_1=217 mm; Profile1_Height=170 mm; Profile1_Length=34 mm; Profile1_Length_2=23 mm  [stored 0.0754593 ft]; Profile_Dia=6 mm  [stored 0.019685 ft]; Profile_Dia_2=6 mm  [stored 0.019685 ft]; Profile_Dia_3=12 mm  [stored 0.0393701 ft]; Profile_height ref=41 mm  [stored 0.134514 ft]; Top_Profile=185 mm; Top_Profile_Ref=190 mm; W=320 mm; W_Ref=314 mm
- 879-0125-00-144006299A0_DN125_PN10/16: Body_Collar_Dia=42 mm  [stored 0.137795 ft]; Body_Collar_Dia_2=29 mm; Body_Flange_Dia=129 mm; Body_Flange_Dia_2=143 mm; Body_Height_1=89 mm; Body_Height_2=50 mm; Body_Height_3=70 mm; Body_Height_4=65 mm; Body_Top_Dia=18 mm  [stored 0.0590551 ft]; Body_Top_Dia_2=15 mm  [stored 0.0492126 ft]; Body_With_Dia=50 mm; Body_With_Dia_1=100 mm; Body_With_Dia_2=108 mm; Bolt_support=308 mm; Bolt_support_2=154 mm; Bolt_support_Dia=12 mm  [stored 0.0393701 ft]; Bolt_support_lenght=83 mm; Bolt_support_lenght_2=93 mm; Bottom_profile=31 mm  [stored 0.101706 ft]; D1=92 mm; D3=125 mm; DN=125 mm; Fillet_Length=6 mm  [stored 0.019685 ft]; Fillet_Length_Ref=18 mm  [stored 0.0590551 ft]; Flange_thickness=19 mm  [stored 0.062336 ft]; H=480 mm; H3_Ref=474 mm; ID=63 mm; L=400 mm; PG_Dia=63 mm; PG_Ref=59 mm; PG_depth=8 mm  [stored 0.0262467 ft]; PG_height=297 mm; PG_height_1=266 mm; PG_ref=73 mm; P_lenght=61 mm; Pilot_Dia_1=28 mm  [stored 0.0918635 ft]; Pilot_Dia_2=55 mm; Pilot_Dia_3=18 mm  [stored 0.0590551 ft]; Pilot_Dia_4=9 mm  [stored 0.0295276 ft]; Pilot_Dia_5=6 mm  [stored 0.019685 ft]; Pilot_top_1=292 mm; Profile1_Height=160 mm; Profile1_Length=34 mm; Profile1_Length_2=23 mm  [stored 0.0754593 ft]; Profile_Dia=6 mm  [stored 0.019685 ft]; Profile_Dia_2=6 mm  [stored 0.019685 ft]; Profile_Dia_3=12 mm  [stored 0.0393701 ft]; Profile_height ref=41 mm  [stored 0.134514 ft]; Top_Profile=185 mm; Top_Profile_Ref=190 mm; W=320 mm; W_Ref=314 mm
- 879-0150-00-14400609999_DN150_PN10/16: Body_Collar_Dia=50 mm; Body_Collar_Dia_2=34 mm; Body_Flange_Dia=155 mm; Body_Flange_Dia_2=171 mm; Body_Height_1=107 mm; Body_Height_2=60 mm; Body_Height_3=30 mm  [stored 0.0984252 ft]; Body_Height_4=75 mm; Body_Top_Dia=22 mm  [stored 0.0721785 ft]; Body_Top_Dia_2=18 mm  [stored 0.0590551 ft]; Body_With_Dia=60 mm; Body_With_Dia_1=120 mm; Body_With_Dia_2=130 mm; Bolt_support=369 mm; Bolt_support_2=185 mm; Bolt_support_Dia=16 mm  [stored 0.0524934 ft]; Bolt_support_lenght=95 mm; Bolt_support_lenght_2=105 mm; Bottom_profile=38 mm; D1=106 mm; D3=143 mm; DN=150 mm; Fillet_Length=8 mm  [stored 0.0262467 ft]; Fillet_Length_Ref=24 mm  [stored 0.0787402 ft]; Flange_thickness=19 mm  [stored 0.062336 ft]; H=383 mm; H3_Ref=375 mm; ID=75 mm; L=480 mm; PG_Dia=50 mm; PG_Ref=71 mm; PG_depth=11 mm; PG_height=287 mm; PG_height_1=262 mm; PG_ref=85 mm; P_lenght=68 mm; Pilot_Dia_1=31 mm  [stored 0.101706 ft]; Pilot_Dia_2=62 mm; Pilot_Dia_3=21 mm  [stored 0.0688976 ft]; Pilot_Dia_4=10 mm  [stored 0.0328084 ft]; Pilot_Dia_5=7 mm  [stored 0.0229659 ft]; Pilot_top_1=244 mm; Profile1_Height=195 mm; Profile1_Length=39 mm  [stored 0.127953 ft]; Profile1_Length_2=26 mm; Profile_Dia=8 mm  [stored 0.0262467 ft]; Profile_Dia_2=8 mm  [stored 0.0262467 ft]; Profile_Dia_3=16 mm  [stored 0.0524934 ft]; Profile_height ref=43 mm  [stored 0.141076 ft]; Top_Profile=222 mm; Top_Profile_Ref=227 mm; W=352 mm; W_Ref=344 mm
- 879-0150-00-14400619999_DN150_PN10/16: Body_Collar_Dia=50 mm; Body_Collar_Dia_2=34 mm; Body_Flange_Dia=155 mm; Body_Flange_Dia_2=171 mm; Body_Height_1=107 mm; Body_Height_2=60 mm; Body_Height_3=30 mm  [stored 0.0984252 ft]; Body_Height_4=75 mm; Body_Top_Dia=22 mm  [stored 0.0721785 ft]; Body_Top_Dia_2=18 mm  [stored 0.0590551 ft]; Body_With_Dia=60 mm; Body_With_Dia_1=120 mm; Body_With_Dia_2=130 mm; Bolt_support=369 mm; Bolt_support_2=185 mm; Bolt_support_Dia=16 mm  [stored 0.0524934 ft]; Bolt_support_lenght=95 mm; Bolt_support_lenght_2=105 mm; Bottom_profile=38 mm; D1=106 mm; D3=143 mm; DN=150 mm; Fillet_Length=8 mm  [stored 0.0262467 ft]; Fillet_Length_Ref=24 mm  [stored 0.0787402 ft]; Flange_thickness=19 mm  [stored 0.062336 ft]; H=383 mm; H3_Ref=375 mm; ID=75 mm; L=480 mm; PG_Dia=50 mm; PG_Ref=71 mm; PG_depth=11 mm; PG_height=287 mm; PG_height_1=262 mm; PG_ref=85 mm; P_lenght=68 mm; Pilot_Dia_1=31 mm  [stored 0.101706 ft]; Pilot_Dia_2=62 mm; Pilot_Dia_3=21 mm  [stored 0.0688976 ft]; Pilot_Dia_4=10 mm  [stored 0.0328084 ft]; Pilot_Dia_5=7 mm  [stored 0.0229659 ft]; Pilot_top_1=248 mm; Profile1_Height=195 mm; Profile1_Length=39 mm  [stored 0.127953 ft]; Profile1_Length_2=26 mm; Profile_Dia=8 mm  [stored 0.0262467 ft]; Profile_Dia_2=8 mm  [stored 0.0262467 ft]; Profile_Dia_3=16 mm  [stored 0.0524934 ft]; Profile_height ref=43 mm  [stored 0.141076 ft]; Top_Profile=222 mm; Top_Profile_Ref=227 mm; W=352 mm; W_Ref=344 mm
- 879-0150-00-14400629999_DN150_PN10/16: Body_Collar_Dia=50 mm; Body_Collar_Dia_2=34 mm; Body_Flange_Dia=155 mm; Body_Flange_Dia_2=171 mm; Body_Height_1=107 mm; Body_Height_2=60 mm; Body_Height_3=30 mm  [stored 0.0984252 ft]; Body_Height_4=75 mm; Body_Top_Dia=22 mm  [stored 0.0721785 ft]; Body_Top_Dia_2=18 mm  [stored 0.0590551 ft]; Body_With_Dia=60 mm; Body_With_Dia_1=120 mm; Body_With_Dia_2=130 mm; Bolt_support=369 mm; Bolt_support_2=185 mm; Bolt_support_Dia=16 mm  [stored 0.0524934 ft]; Bolt_support_lenght=95 mm; Bolt_support_lenght_2=105 mm; Bottom_profile=38 mm; D1=106 mm; D3=143 mm; DN=150 mm; Fillet_Length=8 mm  [stored 0.0262467 ft]; Fillet_Length_Ref=24 mm  [stored 0.0787402 ft]; Flange_thickness=19 mm  [stored 0.062336 ft]; H=383 mm; H3_Ref=375 mm; ID=75 mm; L=480 mm; PG_Dia=50 mm; PG_Ref=71 mm; PG_depth=11 mm; PG_height=287 mm; PG_height_1=262 mm; PG_ref=85 mm; P_lenght=68 mm; Pilot_Dia_1=31 mm  [stored 0.101706 ft]; Pilot_Dia_2=62 mm; Pilot_Dia_3=21 mm  [stored 0.0688976 ft]; Pilot_Dia_4=10 mm  [stored 0.0328084 ft]; Pilot_Dia_5=7 mm  [stored 0.0229659 ft]; Pilot_top_1=244 mm; Profile1_Height=195 mm; Profile1_Length=39 mm  [stored 0.127953 ft]; Profile1_Length_2=26 mm; Profile_Dia=8 mm  [stored 0.0262467 ft]; Profile_Dia_2=8 mm  [stored 0.0262467 ft]; Profile_Dia_3=16 mm  [stored 0.0524934 ft]; Profile_height ref=43 mm  [stored 0.141076 ft]; Top_Profile=222 mm; Top_Profile_Ref=227 mm; W=352 mm; W_Ref=344 mm
- 879-0150-00-144006299A0_DN150_PN10/16: Body_Collar_Dia=50 mm; Body_Collar_Dia_2=34 mm; Body_Flange_Dia=155 mm; Body_Flange_Dia_2=171 mm; Body_Height_1=107 mm; Body_Height_2=60 mm; Body_Height_3=68 mm; Body_Height_4=75 mm; Body_Top_Dia=22 mm  [stored 0.0721785 ft]; Body_Top_Dia_2=18 mm  [stored 0.0590551 ft]; Body_With_Dia=60 mm; Body_With_Dia_1=120 mm; Body_With_Dia_2=130 mm; Bolt_support=369 mm; Bolt_support_2=185 mm; Bolt_support_Dia=16 mm  [stored 0.0524934 ft]; Bolt_support_lenght=95 mm; Bolt_support_lenght_2=105 mm; Bottom_profile=38 mm; D1=106 mm; D3=143 mm; DN=150 mm; Fillet_Length=8 mm  [stored 0.0262467 ft]; Fillet_Length_Ref=24 mm  [stored 0.0787402 ft]; Flange_thickness=19 mm  [stored 0.062336 ft]; H=514 mm; H3_Ref=506 mm; ID=75 mm; L=480 mm; PG_Dia=50 mm; PG_Ref=71 mm; PG_depth=11 mm; PG_height=316 mm; PG_height_1=291 mm; PG_ref=85 mm; P_lenght=68 mm; Pilot_Dia_1=31 mm  [stored 0.101706 ft]; Pilot_Dia_2=62 mm; Pilot_Dia_3=21 mm  [stored 0.0688976 ft]; Pilot_Dia_4=10 mm  [stored 0.0328084 ft]; Pilot_Dia_5=7 mm  [stored 0.0229659 ft]; Pilot_top_1=313 mm; Profile1_Height=195 mm; Profile1_Length=39 mm  [stored 0.127953 ft]; Profile1_Length_2=26 mm; Profile_Dia=8 mm  [stored 0.0262467 ft]; Profile_Dia_2=8 mm  [stored 0.0262467 ft]; Profile_Dia_3=16 mm  [stored 0.0524934 ft]; Profile_height ref=43 mm  [stored 0.141076 ft]; Top_Profile=222 mm; Top_Profile_Ref=227 mm; W=352 mm; W_Ref=344 mm
- 879-0200-00-04400609999_DN200_PN10: Body_Collar_Dia=63 mm; Body_Collar_Dia_2=43 mm  [stored 0.141076 ft]; Body_Flange_Dia=194 mm; Body_Flange_Dia_2=214 mm; Body_Height_1=133 mm; Body_Height_2=75 mm; Body_Height_3=50 mm; Body_Height_4=90 mm; Body_Top_Dia=27 mm; Body_Top_Dia_2=22 mm  [stored 0.0721785 ft]; Body_With_Dia=75 mm; Body_With_Dia_1=150 mm; Body_With_Dia_2=162 mm; Bolt_support=462 mm; Bolt_support_2=231 mm; Bolt_support_Dia=20 mm  [stored 0.0656168 ft]; Bolt_support_lenght=120 mm; Bolt_support_lenght_2=130 mm; Bottom_profile=50 mm; D1=133 mm; D3=170 mm; DN=200 mm; Fillet_Length=10 mm  [stored 0.0328084 ft]; Fillet_Length_Ref=30 mm  [stored 0.0984252 ft]; Flange_thickness=20 mm  [stored 0.0656168 ft]; H=473 mm; H3_Ref=463 mm; ID=100 mm; L=600 mm; PG_Dia=67 mm; PG_Ref=89 mm; PG_depth=14 mm  [stored 0.0459318 ft]; PG_height=352 mm; PG_height_1=319 mm; PG_ref=110 mm; P_lenght=85 mm; Pilot_Dia_1=39 mm  [stored 0.127953 ft]; Pilot_Dia_2=77 mm; Pilot_Dia_3=26 mm; Pilot_Dia_4=13 mm; Pilot_Dia_5=9 mm  [stored 0.0295276 ft]; Pilot_top_1=304 mm; Profile1_Height=238 mm; Profile1_Length=46 mm; Profile1_Length_2=31 mm  [stored 0.101706 ft]; Profile_Dia=10 mm  [stored 0.0328084 ft]; Profile_Dia_2=10 mm  [stored 0.0328084 ft]; Profile_Dia_3=20 mm  [stored 0.0656168 ft]; Profile_height ref=45 mm; Top_Profile=277 mm; Top_Profile_Ref=282 mm; W=438 mm; W_Ref=428 mm
- 879-0200-00-04400619999_DN200_PN10: Body_Collar_Dia=63 mm; Body_Collar_Dia_2=43 mm  [stored 0.141076 ft]; Body_Flange_Dia=194 mm; Body_Flange_Dia_2=214 mm; Body_Height_1=133 mm; Body_Height_2=75 mm; Body_Height_3=55 mm; Body_Height_4=90 mm; Body_Top_Dia=27 mm; Body_Top_Dia_2=22 mm  [stored 0.0721785 ft]; Body_With_Dia=75 mm; Body_With_Dia_1=150 mm; Body_With_Dia_2=162 mm; Bolt_support=462 mm; Bolt_support_2=231 mm; Bolt_support_Dia=20 mm  [stored 0.0656168 ft]; Bolt_support_lenght=120 mm; Bolt_support_lenght_2=130 mm; Bottom_profile=50 mm; D1=133 mm; D3=170 mm; DN=200 mm; Fillet_Length=10 mm  [stored 0.0328084 ft]; Fillet_Length_Ref=30 mm  [stored 0.0984252 ft]; Flange_thickness=20 mm  [stored 0.0656168 ft]; H=473 mm; H3_Ref=463 mm; ID=100 mm; L=600 mm; PG_Dia=67 mm; PG_Ref=89 mm; PG_depth=14 mm  [stored 0.0459318 ft]; PG_height=354 mm; PG_height_1=320 mm; PG_ref=110 mm; P_lenght=85 mm; Pilot_Dia_1=39 mm  [stored 0.127953 ft]; Pilot_Dia_2=77 mm; Pilot_Dia_3=26 mm; Pilot_Dia_4=13 mm; Pilot_Dia_5=9 mm  [stored 0.0295276 ft]; Pilot_top_1=317 mm; Profile1_Height=240 mm; Profile1_Length=46 mm; Profile1_Length_2=31 mm  [stored 0.101706 ft]; Profile_Dia=10 mm  [stored 0.0328084 ft]; Profile_Dia_2=10 mm  [stored 0.0328084 ft]; Profile_Dia_3=20 mm  [stored 0.0656168 ft]; Profile_height ref=45 mm; Top_Profile=277 mm; Top_Profile_Ref=282 mm; W=438 mm; W_Ref=428 mm
- 879-0200-00-04400629999_DN200_PN10: Body_Collar_Dia=63 mm; Body_Collar_Dia_2=43 mm  [stored 0.141076 ft]; Body_Flange_Dia=194 mm; Body_Flange_Dia_2=214 mm; Body_Height_1=133 mm; Body_Height_2=75 mm; Body_Height_3=55 mm; Body_Height_4=90 mm; Body_Top_Dia=27 mm; Body_Top_Dia_2=22 mm  [stored 0.0721785 ft]; Body_With_Dia=75 mm; Body_With_Dia_1=150 mm; Body_With_Dia_2=162 mm; Bolt_support=462 mm; Bolt_support_2=231 mm; Bolt_support_Dia=20 mm  [stored 0.0656168 ft]; Bolt_support_lenght=120 mm; Bolt_support_lenght_2=130 mm; Bottom_profile=50 mm; D1=133 mm; D3=170 mm; DN=200 mm; Fillet_Length=10 mm  [stored 0.0328084 ft]; Fillet_Length_Ref=30 mm  [stored 0.0984252 ft]; Flange_thickness=20 mm  [stored 0.0656168 ft]; H=473 mm; H3_Ref=463 mm; ID=100 mm; L=600 mm; PG_Dia=67 mm; PG_Ref=89 mm; PG_depth=14 mm  [stored 0.0459318 ft]; PG_height=352 mm; PG_height_1=319 mm; PG_ref=110 mm; P_lenght=85 mm; Pilot_Dia_1=39 mm  [stored 0.127953 ft]; Pilot_Dia_2=77 mm; Pilot_Dia_3=26 mm; Pilot_Dia_4=13 mm; Pilot_Dia_5=9 mm  [stored 0.0295276 ft]; Pilot_top_1=304 mm; Profile1_Height=238 mm; Profile1_Length=46 mm; Profile1_Length_2=31 mm  [stored 0.101706 ft]; Profile_Dia=10 mm  [stored 0.0328084 ft]; Profile_Dia_2=10 mm  [stored 0.0328084 ft]; Profile_Dia_3=20 mm  [stored 0.0656168 ft]; Profile_height ref=45 mm; Top_Profile=277 mm; Top_Profile_Ref=282 mm; W=438 mm; W_Ref=428 mm
- 879-0200-00-14400609999_DN200_PN16: Body_Collar_Dia=63 mm; Body_Collar_Dia_2=43 mm  [stored 0.141076 ft]; Body_Flange_Dia=194 mm; Body_Flange_Dia_2=214 mm; Body_Height_1=133 mm; Body_Height_2=75 mm; Body_Height_3=55 mm; Body_Height_4=90 mm; Body_Top_Dia=27 mm; Body_Top_Dia_2=22 mm  [stored 0.0721785 ft]; Body_With_Dia=75 mm; Body_With_Dia_1=150 mm; Body_With_Dia_2=162 mm; Bolt_support=462 mm; Bolt_support_2=231 mm; Bolt_support_Dia=20 mm  [stored 0.0656168 ft]; Bolt_support_lenght=120 mm; Bolt_support_lenght_2=130 mm; Bottom_profile=50 mm; D1=133 mm; D3=170 mm; DN=200 mm; Fillet_Length=10 mm  [stored 0.0328084 ft]; Fillet_Length_Ref=30 mm  [stored 0.0984252 ft]; Flange_thickness=20 mm  [stored 0.0656168 ft]; H=473 mm; H3_Ref=463 mm; ID=100 mm; L=600 mm; PG_Dia=67 mm; PG_Ref=89 mm; PG_depth=14 mm  [stored 0.0459318 ft]; PG_height=354 mm; PG_height_1=320 mm; PG_ref=110 mm; P_lenght=85 mm; Pilot_Dia_1=39 mm  [stored 0.127953 ft]; Pilot_Dia_2=77 mm; Pilot_Dia_3=26 mm; Pilot_Dia_4=13 mm; Pilot_Dia_5=9 mm  [stored 0.0295276 ft]; Pilot_top_1=310 mm; Profile1_Height=240 mm; Profile1_Length=46 mm; Profile1_Length_2=31 mm  [stored 0.101706 ft]; Profile_Dia=10 mm  [stored 0.0328084 ft]; Profile_Dia_2=10 mm  [stored 0.0328084 ft]; Profile_Dia_3=20 mm  [stored 0.0656168 ft]; Profile_height ref=45 mm; Top_Profile=277 mm; Top_Profile_Ref=282 mm; W=438 mm; W_Ref=428 mm
- 879-0200-00-14400619999_DN200_PN16: Body_Collar_Dia=63 mm; Body_Collar_Dia_2=43 mm  [stored 0.141076 ft]; Body_Flange_Dia=194 mm; Body_Flange_Dia_2=214 mm; Body_Height_1=133 mm; Body_Height_2=75 mm; Body_Height_3=55 mm; Body_Height_4=90 mm; Body_Top_Dia=27 mm; Body_Top_Dia_2=22 mm  [stored 0.0721785 ft]; Body_With_Dia=75 mm; Body_With_Dia_1=150 mm; Body_With_Dia_2=162 mm; Bolt_support=462 mm; Bolt_support_2=231 mm; Bolt_support_Dia=20 mm  [stored 0.0656168 ft]; Bolt_support_lenght=120 mm; Bolt_support_lenght_2=130 mm; Bottom_profile=50 mm; D1=133 mm; D3=170 mm; DN=200 mm; Fillet_Length=10 mm  [stored 0.0328084 ft]; Fillet_Length_Ref=30 mm  [stored 0.0984252 ft]; Flange_thickness=20 mm  [stored 0.0656168 ft]; H=473 mm; H3_Ref=463 mm; ID=100 mm; L=600 mm; PG_Dia=67 mm; PG_Ref=89 mm; PG_depth=14 mm  [stored 0.0459318 ft]; PG_height=352 mm; PG_height_1=319 mm; PG_ref=110 mm; P_lenght=85 mm; Pilot_Dia_1=39 mm  [stored 0.127953 ft]; Pilot_Dia_2=77 mm; Pilot_Dia_3=26 mm; Pilot_Dia_4=13 mm; Pilot_Dia_5=9 mm  [stored 0.0295276 ft]; Pilot_top_1=304 mm; Profile1_Height=238 mm; Profile1_Length=46 mm; Profile1_Length_2=31 mm  [stored 0.101706 ft]; Profile_Dia=10 mm  [stored 0.0328084 ft]; Profile_Dia_2=10 mm  [stored 0.0328084 ft]; Profile_Dia_3=20 mm  [stored 0.0656168 ft]; Profile_height ref=45 mm; Top_Profile=277 mm; Top_Profile_Ref=282 mm; W=438 mm; W_Ref=428 mm
- 879-0200-00-14400629999_DN200_PN16: Body_Collar_Dia=63 mm; Body_Collar_Dia_2=43 mm  [stored 0.141076 ft]; Body_Flange_Dia=194 mm; Body_Flange_Dia_2=214 mm; Body_Height_1=133 mm; Body_Height_2=75 mm; Body_Height_3=55 mm; Body_Height_4=90 mm; Body_Top_Dia=27 mm; Body_Top_Dia_2=22 mm  [stored 0.0721785 ft]; Body_With_Dia=75 mm; Body_With_Dia_1=150 mm; Body_With_Dia_2=162 mm; Bolt_support=462 mm; Bolt_support_2=231 mm; Bolt_support_Dia=20 mm  [stored 0.0656168 ft]; Bolt_support_lenght=120 mm; Bolt_support_lenght_2=130 mm; Bottom_profile=50 mm; D1=133 mm; D3=170 mm; DN=201 mm; Fillet_Length=10 mm  [stored 0.0328084 ft]; Fillet_Length_Ref=30 mm  [stored 0.0984252 ft]; Flange_thickness=20 mm  [stored 0.0656168 ft]; H=473 mm; H3_Ref=463 mm; ID=100 mm; L=600 mm; PG_Dia=67 mm; PG_Ref=89 mm; PG_depth=14 mm  [stored 0.0459318 ft]; PG_height=354 mm; PG_height_1=320 mm; PG_ref=110 mm; P_lenght=85 mm; Pilot_Dia_1=39 mm  [stored 0.127953 ft]; Pilot_Dia_2=77 mm; Pilot_Dia_3=26 mm; Pilot_Dia_4=13 mm; Pilot_Dia_5=9 mm  [stored 0.0295276 ft]; Pilot_top_1=317 mm; Profile1_Height=240 mm; Profile1_Length=46 mm; Profile1_Length_2=31 mm  [stored 0.101706 ft]; Profile_Dia=10 mm  [stored 0.0328084 ft]; Profile_Dia_2=10 mm  [stored 0.0328084 ft]; Profile_Dia_3=20 mm  [stored 0.0656168 ft]; Profile_height ref=45 mm; Top_Profile=277 mm; Top_Profile_Ref=282 mm; W=438 mm; W_Ref=428 mm
- 879-0200-00-144006299A0_DN200_PN16: Body_Collar_Dia=63 mm; Body_Collar_Dia_2=43 mm  [stored 0.141076 ft]; Body_Flange_Dia=194 mm; Body_Flange_Dia_2=214 mm; Body_Height_1=133 mm; Body_Height_2=75 mm; Body_Height_3=75 mm; Body_Height_4=90 mm; Body_Top_Dia=27 mm; Body_Top_Dia_2=22 mm  [stored 0.0721785 ft]; Body_With_Dia=75 mm; Body_With_Dia_1=150 mm; Body_With_Dia_2=162 mm; Bolt_support=462 mm; Bolt_support_2=231 mm; Bolt_support_Dia=20 mm  [stored 0.0656168 ft]; Bolt_support_lenght=120 mm; Bolt_support_lenght_2=130 mm; Bottom_profile=50 mm; D1=133 mm; D3=170 mm; DN=201 mm; Fillet_Length=10 mm  [stored 0.0328084 ft]; Fillet_Length_Ref=30 mm  [stored 0.0984252 ft]; Flange_thickness=20 mm  [stored 0.0656168 ft]; H=688 mm; H3_Ref=678 mm; ID=100 mm; L=600 mm; PG_Dia=67 mm; PG_Ref=89 mm; PG_depth=14 mm  [stored 0.0459318 ft]; PG_height=401 mm; PG_height_1=367 mm; PG_ref=110 mm; P_lenght=85 mm; Pilot_Dia_1=39 mm  [stored 0.127953 ft]; Pilot_Dia_2=77 mm; Pilot_Dia_3=26 mm; Pilot_Dia_4=13 mm; Pilot_Dia_5=9 mm  [stored 0.0295276 ft]; Pilot_top_1=412 mm; Profile1_Height=238 mm; Profile1_Length=46 mm; Profile1_Length_2=31 mm  [stored 0.101706 ft]; Profile_Dia=10 mm  [stored 0.0328084 ft]; Profile_Dia_2=10 mm  [stored 0.0328084 ft]; Profile_Dia_3=20 mm  [stored 0.0656168 ft]; Profile_height ref=45 mm; Top_Profile=277 mm; Top_Profile_Ref=282 mm; W=438 mm; W_Ref=428 mm
- 879-0250-00-04400609999_DN250_PN10: Body_Collar_Dia=76 mm; Body_Collar_Dia_2=52 mm; Body_Flange_Dia=235 mm; Body_Flange_Dia_2=261 mm; Body_Height_1=162 mm; Body_Height_2=91 mm; Body_Height_3=81 mm; Body_Height_4=106 mm; Body_Top_Dia=33 mm; Body_Top_Dia_2=27 mm; Body_With_Dia=91 mm; Body_With_Dia_1=183 mm; Body_With_Dia_2=197 mm; Bolt_support=562 mm; Bolt_support_2=281 mm; Bolt_support_Dia=20 mm  [stored 0.0656168 ft]; Bolt_support_lenght=145 mm; Bolt_support_lenght_2=155 mm; Bottom_profile=63 mm; D1=160 mm; D3=198 mm; DN=250 mm; Fillet_Length=10 mm  [stored 0.0328084 ft]; Fillet_Length_Ref=30 mm  [stored 0.0984252 ft]; Flange_thickness=22 mm  [stored 0.0721785 ft]; H=617 mm; H3_Ref=607 mm; ID=125 mm; L=730 mm; PG_Dia=83 mm; PG_Ref=108 mm; PG_depth=14 mm  [stored 0.0459318 ft]; PG_height=437 mm; PG_height_1=395 mm; PG_ref=135 mm; P_lenght=101 mm; Pilot_Dia_1=46 mm; Pilot_Dia_2=92 mm; Pilot_Dia_3=31 mm  [stored 0.101706 ft]; Pilot_Dia_4=15 mm  [stored 0.0492126 ft]; Pilot_Dia_5=10 mm  [stored 0.0328084 ft]; Pilot_top_1=390 mm; Profile1_Height=292 mm; Profile1_Length=53 mm; Profile1_Length_2=36 mm  [stored 0.11811 ft]; Profile_Dia=10 mm  [stored 0.0328084 ft]; Profile_Dia_2=10 mm  [stored 0.0328084 ft]; Profile_Dia_3=20 mm  [stored 0.0656168 ft]; Profile_height ref=45 mm; Top_Profile=337 mm; Top_Profile_Ref=342 mm; W=514 mm; W_Ref=504 mm
- 879-0250-00-04400619999_DN250_PN10: Body_Collar_Dia=76 mm; Body_Collar_Dia_2=52 mm; Body_Flange_Dia=235 mm; Body_Flange_Dia_2=261 mm; Body_Height_1=162 mm; Body_Height_2=91 mm; Body_Height_3=105 mm; Body_Height_4=106 mm; Body_Top_Dia=33 mm; Body_Top_Dia_2=27 mm; Body_With_Dia=91 mm; Body_With_Dia_1=183 mm; Body_With_Dia_2=197 mm; Bolt_support=562 mm; Bolt_support_2=281 mm; Bolt_support_Dia=20 mm  [stored 0.0656168 ft]; Bolt_support_lenght=145 mm; Bolt_support_lenght_2=155 mm; Bottom_profile=63 mm; D1=160 mm; D3=198 mm; DN=250 mm; Fillet_Length=10 mm  [stored 0.0328084 ft]; Fillet_Length_Ref=30 mm  [stored 0.0984252 ft]; Flange_thickness=22 mm  [stored 0.0721785 ft]; H=617 mm; H3_Ref=607 mm; ID=125 mm; L=730 mm; PG_Dia=83 mm; PG_Ref=108 mm; PG_depth=14 mm  [stored 0.0459318 ft]; PG_height=439 mm; PG_height_1=397 mm; PG_ref=135 mm; P_lenght=101 mm; Pilot_Dia_1=46 mm; Pilot_Dia_2=92 mm; Pilot_Dia_3=31 mm  [stored 0.101706 ft]; Pilot_Dia_4=15 mm  [stored 0.0492126 ft]; Pilot_Dia_5=10 mm  [stored 0.0328084 ft]; Pilot_top_1=401 mm; Profile1_Height=295 mm; Profile1_Length=53 mm; Profile1_Length_2=36 mm  [stored 0.11811 ft]; Profile_Dia=10 mm  [stored 0.0328084 ft]; Profile_Dia_2=10 mm  [stored 0.0328084 ft]; Profile_Dia_3=20 mm  [stored 0.0656168 ft]; Profile_height ref=45 mm; Top_Profile=337 mm; Top_Profile_Ref=342 mm; W=514 mm; W_Ref=504 mm
- 879-0250-00-04400629999_DN250_PN10: Body_Collar_Dia=76 mm; Body_Collar_Dia_2=52 mm; Body_Flange_Dia=235 mm; Body_Flange_Dia_2=261 mm; Body_Height_1=162 mm; Body_Height_2=91 mm; Body_Height_3=81 mm; Body_Height_4=106 mm; Body_Top_Dia=33 mm; Body_Top_Dia_2=27 mm; Body_With_Dia=91 mm; Body_With_Dia_1=183 mm; Body_With_Dia_2=197 mm; Bolt_support=562 mm; Bolt_support_2=281 mm; Bolt_support_Dia=20 mm  [stored 0.0656168 ft]; Bolt_support_lenght=145 mm; Bolt_support_lenght_2=155 mm; Bottom_profile=63 mm; D1=160 mm; D3=198 mm; DN=250 mm; Fillet_Length=10 mm  [stored 0.0328084 ft]; Fillet_Length_Ref=30 mm  [stored 0.0984252 ft]; Flange_thickness=22 mm  [stored 0.0721785 ft]; H=617 mm; H3_Ref=607 mm; ID=125 mm; L=730 mm; PG_Dia=83 mm; PG_Ref=108 mm; PG_depth=14 mm  [stored 0.0459318 ft]; PG_height=443 mm; PG_height_1=401 mm; PG_ref=135 mm; P_lenght=103 mm; Pilot_Dia_1=47 mm; Pilot_Dia_2=94 mm; Pilot_Dia_3=31 mm  [stored 0.101706 ft]; Pilot_Dia_4=16 mm  [stored 0.0524934 ft]; Pilot_Dia_5=10 mm  [stored 0.0328084 ft]; Pilot_top_1=390 mm; Profile1_Height=300 mm; Profile1_Length=53 mm; Profile1_Length_2=36 mm  [stored 0.11811 ft]; Profile_Dia=10 mm  [stored 0.0328084 ft]; Profile_Dia_2=10 mm  [stored 0.0328084 ft]; Profile_Dia_3=20 mm  [stored 0.0656168 ft]; Profile_height ref=45 mm; Top_Profile=337 mm; Top_Profile_Ref=342 mm; W=514 mm; W_Ref=504 mm
- 879-0250-00-14400609999_DN250_PN16: Body_Collar_Dia=76 mm; Body_Collar_Dia_2=52 mm; Body_Flange_Dia=235 mm; Body_Flange_Dia_2=261 mm; Body_Height_1=162 mm; Body_Height_2=91 mm; Body_Height_3=81 mm; Body_Height_4=106 mm; Body_Top_Dia=33 mm; Body_Top_Dia_2=27 mm; Body_With_Dia=91 mm; Body_With_Dia_1=183 mm; Body_With_Dia_2=197 mm; Bolt_support=562 mm; Bolt_support_2=281 mm; Bolt_support_Dia=20 mm  [stored 0.0656168 ft]; Bolt_support_lenght=145 mm; Bolt_support_lenght_2=155 mm; Bottom_profile=63 mm; D1=160 mm; D3=203 mm; DN=250 mm; Fillet_Length=10 mm  [stored 0.0328084 ft]; Fillet_Length_Ref=30 mm  [stored 0.0984252 ft]; Flange_thickness=22 mm  [stored 0.0721785 ft]; H=617 mm; H3_Ref=607 mm; ID=125 mm; L=730 mm; PG_Dia=83 mm; PG_Ref=108 mm; PG_depth=14 mm  [stored 0.0459318 ft]; PG_height=453 mm; PG_height_1=412 mm; PG_ref=135 mm; P_lenght=103 mm; Pilot_Dia_1=47 mm; Pilot_Dia_2=94 mm; Pilot_Dia_3=31 mm  [stored 0.101706 ft]; Pilot_Dia_4=16 mm  [stored 0.0524934 ft]; Pilot_Dia_5=10 mm  [stored 0.0328084 ft]; Pilot_top_1=387 mm; Profile1_Height=315 mm; Profile1_Length=55 mm; Profile1_Length_2=36 mm  [stored 0.11811 ft]; Profile_Dia=10 mm  [stored 0.0328084 ft]; Profile_Dia_2=10 mm  [stored 0.0328084 ft]; Profile_Dia_3=20 mm  [stored 0.0656168 ft]; Profile_height ref=45 mm; Top_Profile=337 mm; Top_Profile_Ref=342 mm; W=514 mm; W_Ref=504 mm
- 879-0250-00-14400619999_DN250_PN16: Body_Collar_Dia=76 mm; Body_Collar_Dia_2=52 mm; Body_Flange_Dia=235 mm; Body_Flange_Dia_2=261 mm; Body_Height_1=162 mm; Body_Height_2=91 mm; Body_Height_3=81 mm; Body_Height_4=106 mm; Body_Top_Dia=33 mm; Body_Top_Dia_2=27 mm; Body_With_Dia=91 mm; Body_With_Dia_1=183 mm; Body_With_Dia_2=197 mm; Bolt_support=562 mm; Bolt_support_2=281 mm; Bolt_support_Dia=20 mm  [stored 0.0656168 ft]; Bolt_support_lenght=145 mm; Bolt_support_lenght_2=155 mm; Bottom_profile=63 mm; D1=160 mm; D3=203 mm; DN=250 mm; Fillet_Length=10 mm  [stored 0.0328084 ft]; Fillet_Length_Ref=30 mm  [stored 0.0984252 ft]; Flange_thickness=22 mm  [stored 0.0721785 ft]; H=617 mm; H3_Ref=607 mm; ID=125 mm; L=730 mm; PG_Dia=83 mm; PG_Ref=108 mm; PG_depth=14 mm  [stored 0.0459318 ft]; PG_height=436 mm; PG_height_1=394 mm; PG_ref=135 mm; P_lenght=101 mm; Pilot_Dia_1=46 mm; Pilot_Dia_2=92 mm; Pilot_Dia_3=31 mm  [stored 0.101706 ft]; Pilot_Dia_4=15 mm  [stored 0.0492126 ft]; Pilot_Dia_5=10 mm  [stored 0.0328084 ft]; Pilot_top_1=387 mm; Profile1_Height=292 mm; Profile1_Length=55 mm; Profile1_Length_2=36 mm  [stored 0.11811 ft]; Profile_Dia=10 mm  [stored 0.0328084 ft]; Profile_Dia_2=10 mm  [stored 0.0328084 ft]; Profile_Dia_3=20 mm  [stored 0.0656168 ft]; Profile_height ref=45 mm; Top_Profile=337 mm; Top_Profile_Ref=342 mm; W=514 mm; W_Ref=504 mm
- 879-0250-00-14400629999_DN250_PN16: Body_Collar_Dia=76 mm; Body_Collar_Dia_2=52 mm; Body_Flange_Dia=235 mm; Body_Flange_Dia_2=261 mm; Body_Height_1=162 mm; Body_Height_2=91 mm; Body_Height_3=105 mm; Body_Height_4=106 mm; Body_Top_Dia=33 mm; Body_Top_Dia_2=27 mm; Body_With_Dia=91 mm; Body_With_Dia_1=183 mm; Body_With_Dia_2=197 mm; Bolt_support=562 mm; Bolt_support_2=281 mm; Bolt_support_Dia=20 mm  [stored 0.0656168 ft]; Bolt_support_lenght=145 mm; Bolt_support_lenght_2=155 mm; Bottom_profile=63 mm; D1=160 mm; D3=203 mm; DN=251 mm; Fillet_Length=10 mm  [stored 0.0328084 ft]; Fillet_Length_Ref=30 mm  [stored 0.0984252 ft]; Flange_thickness=22 mm  [stored 0.0721785 ft]; H=617 mm; H3_Ref=607 mm; ID=125 mm; L=730 mm; PG_Dia=84 mm; PG_Ref=108 mm; PG_depth=14 mm  [stored 0.0459318 ft]; PG_height=438 mm; PG_height_1=396 mm; PG_ref=135 mm; P_lenght=101 mm; Pilot_Dia_1=46 mm; Pilot_Dia_2=92 mm; Pilot_Dia_3=31 mm  [stored 0.101706 ft]; Pilot_Dia_4=15 mm  [stored 0.0492126 ft]; Pilot_Dia_5=10 mm  [stored 0.0328084 ft]; Pilot_top_1=399 mm; Profile1_Height=295 mm; Profile1_Length=55 mm; Profile1_Length_2=36 mm  [stored 0.11811 ft]; Profile_Dia=10 mm  [stored 0.0328084 ft]; Profile_Dia_2=10 mm  [stored 0.0328084 ft]; Profile_Dia_3=20 mm  [stored 0.0656168 ft]; Profile_height ref=45 mm; Top_Profile=337 mm; Top_Profile_Ref=342 mm; W=514 mm; W_Ref=504 mm
- 879-0250-00-144006299A0_DN250_PN16: Body_Collar_Dia=76 mm; Body_Collar_Dia_2=52 mm; Body_Flange_Dia=235 mm; Body_Flange_Dia_2=261 mm; Body_Height_1=162 mm; Body_Height_2=91 mm; Body_Height_3=81 mm; Body_Height_4=106 mm; Body_Top_Dia=33 mm; Body_Top_Dia_2=27 mm; Body_With_Dia=91 mm; Body_With_Dia_1=183 mm; Body_With_Dia_2=197 mm; Bolt_support=562 mm; Bolt_support_2=281 mm; Bolt_support_Dia=20 mm  [stored 0.0656168 ft]; Bolt_support_lenght=145 mm; Bolt_support_lenght_2=155 mm; Bottom_profile=63 mm; D1=160 mm; D3=203 mm; DN=251 mm; Fillet_Length=10 mm  [stored 0.0328084 ft]; Fillet_Length_Ref=30 mm  [stored 0.0984252 ft]; Flange_thickness=22 mm  [stored 0.0721785 ft]; H=806 mm; H3_Ref=796 mm; ID=125 mm; L=730 mm; PG_Dia=84 mm; PG_Ref=108 mm; PG_depth=14 mm  [stored 0.0459318 ft]; PG_height=485 mm; PG_height_1=443 mm; PG_ref=135 mm; P_lenght=103 mm; Pilot_Dia_1=47 mm; Pilot_Dia_2=94 mm; Pilot_Dia_3=31 mm  [stored 0.101706 ft]; Pilot_Dia_4=16 mm  [stored 0.0524934 ft]; Pilot_Dia_5=10 mm  [stored 0.0328084 ft]; Pilot_top_1=482 mm; Profile1_Height=300 mm; Profile1_Length=55 mm; Profile1_Length_2=36 mm  [stored 0.11811 ft]; Profile_Dia=10 mm  [stored 0.0328084 ft]; Profile_Dia_2=10 mm  [stored 0.0328084 ft]; Profile_Dia_3=20 mm  [stored 0.0656168 ft]; Profile_height ref=45 mm; Top_Profile=337 mm; Top_Profile_Ref=342 mm; W=514 mm; W_Ref=504 mm
- 879-0300-00-04400609999_DN300_PN10: Body_Collar_Dia=89 mm; Body_Collar_Dia_2=61 mm; Body_Flange_Dia=274 mm; Body_Flange_Dia_2=304 mm; Body_Height_1=189 mm; Body_Height_2=106 mm; Body_Height_3=95 mm; Body_Height_4=121 mm; Body_Top_Dia=38 mm; Body_Top_Dia_2=32 mm; Body_With_Dia=106 mm; Body_With_Dia_1=213 mm; Body_With_Dia_2=230 mm; Bolt_support=654 mm; Bolt_support_2=327 mm; Bolt_support_Dia=20 mm  [stored 0.0656168 ft]; Bolt_support_lenght=170 mm; Bolt_support_lenght_2=180 mm; Bottom_profile=75 mm; D1=185 mm; D3=223 mm; DN=300 mm; Fillet_Length=10 mm  [stored 0.0328084 ft]; Fillet_Length_Ref=30 mm  [stored 0.0984252 ft]; Flange_thickness=25 mm  [stored 0.082021 ft]; H=694 mm; H3_Ref=684 mm; ID=150 mm; L=850 mm; PG_Dia=100 mm; PG_Ref=126 mm; PG_depth=14 mm  [stored 0.0459318 ft]; PG_height=491 mm; PG_height_1=441 mm; PG_ref=160 mm; P_lenght=116 mm; Pilot_Dia_1=53 mm; Pilot_Dia_2=105 mm; Pilot_Dia_3=35 mm  [stored 0.114829 ft]; Pilot_Dia_4=18 mm  [stored 0.0590551 ft]; Pilot_Dia_5=12 mm  [stored 0.0393701 ft]; Pilot_top_1=445 mm; Profile1_Height=326 mm; Profile1_Length=60 mm; Profile1_Length_2=40 mm  [stored 0.131234 ft]; Profile_Dia=10 mm  [stored 0.0328084 ft]; Profile_Dia_2=10 mm  [stored 0.0328084 ft]; Profile_Dia_3=20 mm  [stored 0.0656168 ft]; Profile_height ref=45 mm; Top_Profile=392 mm; Top_Profile_Ref=397 mm; W=562 mm; W_Ref=552 mm
- 879-0300-00-04400619999_DN300_PN10: Body_Collar_Dia=89 mm; Body_Collar_Dia_2=61 mm; Body_Flange_Dia=274 mm; Body_Flange_Dia_2=304 mm; Body_Height_1=189 mm; Body_Height_2=106 mm; Body_Height_3=106 mm; Body_Height_4=121 mm; Body_Top_Dia=38 mm; Body_Top_Dia_2=32 mm; Body_With_Dia=106 mm; Body_With_Dia_1=213 mm; Body_With_Dia_2=230 mm; Bolt_support=654 mm; Bolt_support_2=327 mm; Bolt_support_Dia=20 mm  [stored 0.0656168 ft]; Bolt_support_lenght=170 mm; Bolt_support_lenght_2=180 mm; Bottom_profile=75 mm; D1=185 mm; D3=223 mm; DN=300 mm; Fillet_Length=10 mm  [stored 0.0328084 ft]; Fillet_Length_Ref=30 mm  [stored 0.0984252 ft]; Flange_thickness=25 mm  [stored 0.082021 ft]; H=694 mm; H3_Ref=684 mm; ID=150 mm; L=850 mm; PG_Dia=100 mm; PG_Ref=126 mm; PG_depth=14 mm  [stored 0.0459318 ft]; PG_height=522 mm; PG_height_1=472 mm; PG_ref=160 mm; P_lenght=116 mm; Pilot_Dia_1=53 mm; Pilot_Dia_2=105 mm; Pilot_Dia_3=35 mm  [stored 0.114829 ft]; Pilot_Dia_4=18 mm  [stored 0.0590551 ft]; Pilot_Dia_5=12 mm  [stored 0.0393701 ft]; Pilot_top_1=451 mm; Profile1_Height=365 mm; Profile1_Length=60 mm; Profile1_Length_2=40 mm  [stored 0.131234 ft]; Profile_Dia=10 mm  [stored 0.0328084 ft]; Profile_Dia_2=10 mm  [stored 0.0328084 ft]; Profile_Dia_3=20 mm  [stored 0.0656168 ft]; Profile_height ref=45 mm; Top_Profile=392 mm; Top_Profile_Ref=397 mm; W=562 mm; W_Ref=552 mm
- 879-0300-00-04400629999_DN300_PN10: Body_Collar_Dia=89 mm; Body_Collar_Dia_2=61 mm; Body_Flange_Dia=274 mm; Body_Flange_Dia_2=304 mm; Body_Height_1=189 mm; Body_Height_2=106 mm; Body_Height_3=95 mm; Body_Height_4=121 mm; Body_Top_Dia=38 mm; Body_Top_Dia_2=32 mm; Body_With_Dia=106 mm; Body_With_Dia_1=213 mm; Body_With_Dia_2=230 mm; Bolt_support=654 mm; Bolt_support_2=327 mm; Bolt_support_Dia=20 mm  [stored 0.0656168 ft]; Bolt_support_lenght=170 mm; Bolt_support_lenght_2=180 mm; Bottom_profile=75 mm; D1=185 mm; D3=223 mm; DN=300 mm; Fillet_Length=10 mm  [stored 0.0328084 ft]; Fillet_Length_Ref=30 mm  [stored 0.0984252 ft]; Flange_thickness=25 mm  [stored 0.082021 ft]; H=694 mm; H3_Ref=684 mm; ID=150 mm; L=850 mm; PG_Dia=100 mm; PG_Ref=126 mm; PG_depth=14 mm  [stored 0.0459318 ft]; PG_height=505 mm; PG_height_1=455 mm; PG_ref=160 mm; P_lenght=120 mm; Pilot_Dia_1=55 mm; Pilot_Dia_2=109 mm; Pilot_Dia_3=36 mm  [stored 0.11811 ft]; Pilot_Dia_4=18 mm  [stored 0.0590551 ft]; Pilot_Dia_5=12 mm  [stored 0.0393701 ft]; Pilot_top_1=441 mm; Profile1_Height=345 mm; Profile1_Length=60 mm; Profile1_Length_2=40 mm  [stored 0.131234 ft]; Profile_Dia=10 mm  [stored 0.0328084 ft]; Profile_Dia_2=10 mm  [stored 0.0328084 ft]; Profile_Dia_3=20 mm  [stored 0.0656168 ft]; Profile_height ref=45 mm; Top_Profile=392 mm; Top_Profile_Ref=397 mm; W=562 mm; W_Ref=552 mm
- 879-0300-00-14400609999_DN300_PN16: Body_Collar_Dia=89 mm; Body_Collar_Dia_2=61 mm; Body_Flange_Dia=274 mm; Body_Flange_Dia_2=304 mm; Body_Height_1=189 mm; Body_Height_2=106 mm; Body_Height_3=95 mm; Body_Height_4=121 mm; Body_Top_Dia=38 mm; Body_Top_Dia_2=32 mm; Body_With_Dia=106 mm; Body_With_Dia_1=213 mm; Body_With_Dia_2=230 mm; Bolt_support=654 mm; Bolt_support_2=327 mm; Bolt_support_Dia=20 mm  [stored 0.0656168 ft]; Bolt_support_lenght=170 mm; Bolt_support_lenght_2=180 mm; Bottom_profile=75 mm; D1=185 mm; D3=230 mm; DN=300 mm; Fillet_Length=10 mm  [stored 0.0328084 ft]; Fillet_Length_Ref=30 mm  [stored 0.0984252 ft]; Flange_thickness=25 mm  [stored 0.082021 ft]; H=694 mm; H3_Ref=684 mm; ID=150 mm; L=850 mm; PG_Dia=100 mm; PG_Ref=126 mm; PG_depth=14 mm  [stored 0.0459318 ft]; PG_height=490 mm; PG_height_1=440 mm; PG_ref=160 mm; P_lenght=116 mm; Pilot_Dia_1=53 mm; Pilot_Dia_2=105 mm; Pilot_Dia_3=35 mm  [stored 0.114829 ft]; Pilot_Dia_4=18 mm  [stored 0.0590551 ft]; Pilot_Dia_5=12 mm  [stored 0.0393701 ft]; Pilot_top_1=441 mm; Profile1_Height=326 mm; Profile1_Length=62 mm; Profile1_Length_2=41 mm  [stored 0.134514 ft]; Profile_Dia=10 mm  [stored 0.0328084 ft]; Profile_Dia_2=10 mm  [stored 0.0328084 ft]; Profile_Dia_3=20 mm  [stored 0.0656168 ft]; Profile_height ref=45 mm; Top_Profile=392 mm; Top_Profile_Ref=397 mm; W=562 mm; W_Ref=552 mm
- 879-0300-00-14400619999_DN300_PN16: Body_Collar_Dia=89 mm; Body_Collar_Dia_2=61 mm; Body_Flange_Dia=274 mm; Body_Flange_Dia_2=304 mm; Body_Height_1=189 mm; Body_Height_2=106 mm; Body_Height_3=106 mm; Body_Height_4=121 mm; Body_Top_Dia=38 mm; Body_Top_Dia_2=32 mm; Body_With_Dia=106 mm; Body_With_Dia_1=213 mm; Body_With_Dia_2=230 mm; Bolt_support=654 mm; Bolt_support_2=327 mm; Bolt_support_Dia=20 mm  [stored 0.0656168 ft]; Bolt_support_lenght=170 mm; Bolt_support_lenght_2=180 mm; Bottom_profile=75 mm; D1=185 mm; D3=230 mm; DN=301 mm; Fillet_Length=10 mm  [stored 0.0328084 ft]; Fillet_Length_Ref=30 mm  [stored 0.0984252 ft]; Flange_thickness=25 mm  [stored 0.082021 ft]; H=694 mm; H3_Ref=684 mm; ID=150 mm; L=850 mm; PG_Dia=100 mm; PG_Ref=126 mm; PG_depth=14 mm  [stored 0.0459318 ft]; PG_height=520 mm; PG_height_1=470 mm; PG_ref=160 mm; P_lenght=116 mm; Pilot_Dia_1=53 mm; Pilot_Dia_2=105 mm; Pilot_Dia_3=35 mm  [stored 0.114829 ft]; Pilot_Dia_4=18 mm  [stored 0.0590551 ft]; Pilot_Dia_5=12 mm  [stored 0.0393701 ft]; Pilot_top_1=447 mm; Profile1_Height=365 mm; Profile1_Length=62 mm; Profile1_Length_2=41 mm  [stored 0.134514 ft]; Profile_Dia=10 mm  [stored 0.0328084 ft]; Profile_Dia_2=10 mm  [stored 0.0328084 ft]; Profile_Dia_3=20 mm  [stored 0.0656168 ft]; Profile_height ref=45 mm; Top_Profile=392 mm; Top_Profile_Ref=397 mm; W=562 mm; W_Ref=552 mm
- 879-0300-00-14400629999_DN300_PN16: Body_Collar_Dia=89 mm; Body_Collar_Dia_2=61 mm; Body_Flange_Dia=274 mm; Body_Flange_Dia_2=304 mm; Body_Height_1=189 mm; Body_Height_2=106 mm; Body_Height_3=106 mm; Body_Height_4=121 mm; Body_Top_Dia=38 mm; Body_Top_Dia_2=32 mm; Body_With_Dia=106 mm; Body_With_Dia_1=213 mm; Body_With_Dia_2=230 mm; Bolt_support=654 mm; Bolt_support_2=327 mm; Bolt_support_Dia=20 mm  [stored 0.0656168 ft]; Bolt_support_lenght=170 mm; Bolt_support_lenght_2=180 mm; Bottom_profile=75 mm; D1=185 mm; D3=230 mm; DN=301 mm; Fillet_Length=10 mm  [stored 0.0328084 ft]; Fillet_Length_Ref=30 mm  [stored 0.0984252 ft]; Flange_thickness=25 mm  [stored 0.082021 ft]; H=694 mm; H3_Ref=684 mm; ID=150 mm; L=850 mm; PG_Dia=100 mm; PG_Ref=126 mm; PG_depth=14 mm  [stored 0.0459318 ft]; PG_height=520 mm; PG_height_1=470 mm; PG_ref=160 mm; P_lenght=116 mm; Pilot_Dia_1=53 mm; Pilot_Dia_2=105 mm; Pilot_Dia_3=35 mm  [stored 0.114829 ft]; Pilot_Dia_4=18 mm  [stored 0.0590551 ft]; Pilot_Dia_5=12 mm  [stored 0.0393701 ft]; Pilot_top_1=447 mm; Profile1_Height=365 mm; Profile1_Length=62 mm; Profile1_Length_2=41 mm  [stored 0.134514 ft]; Profile_Dia=10 mm  [stored 0.0328084 ft]; Profile_Dia_2=10 mm  [stored 0.0328084 ft]; Profile_Dia_3=20 mm  [stored 0.0656168 ft]; Profile_height ref=45 mm; Top_Profile=392 mm; Top_Profile_Ref=397 mm; W=562 mm; W_Ref=552 mm
- 879-0300-00-144006299A0_DN300_PN16: Body_Collar_Dia=89 mm; Body_Collar_Dia_2=61 mm; Body_Flange_Dia=274 mm; Body_Flange_Dia_2=304 mm; Body_Height_1=189 mm; Body_Height_2=106 mm; Body_Height_3=95 mm; Body_Height_4=121 mm; Body_Top_Dia=38 mm; Body_Top_Dia_2=32 mm; Body_With_Dia=106 mm; Body_With_Dia_1=213 mm; Body_With_Dia_2=230 mm; Bolt_support=654 mm; Bolt_support_2=327 mm; Bolt_support_Dia=20 mm  [stored 0.0656168 ft]; Bolt_support_lenght=170 mm; Bolt_support_lenght_2=180 mm; Bottom_profile=75 mm; D1=185 mm; D3=230 mm; DN=301 mm; Fillet_Length=10 mm  [stored 0.0328084 ft]; Fillet_Length_Ref=30 mm  [stored 0.0984252 ft]; Flange_thickness=25 mm  [stored 0.082021 ft]; H=881 mm; H3_Ref=871 mm; ID=150 mm; L=850 mm; PG_Dia=100 mm; PG_Ref=126 mm; PG_depth=14 mm  [stored 0.0459318 ft]; PG_height=547 mm; PG_height_1=497 mm; PG_ref=160 mm; P_lenght=120 mm; Pilot_Dia_1=55 mm; Pilot_Dia_2=109 mm; Pilot_Dia_3=36 mm  [stored 0.11811 ft]; Pilot_Dia_4=18 mm  [stored 0.0590551 ft]; Pilot_Dia_5=12 mm  [stored 0.0393701 ft]; Pilot_top_1=535 mm; Profile1_Height=345 mm; Profile1_Length=62 mm; Profile1_Length_2=41 mm  [stored 0.134514 ft]; Profile_Dia=10 mm  [stored 0.0328084 ft]; Profile_Dia_2=10 mm  [stored 0.0328084 ft]; Profile_Dia_3=20 mm  [stored 0.0656168 ft]; Profile_height ref=45 mm; Top_Profile=392 mm; Top_Profile_Ref=397 mm; W=562 mm; W_Ref=552 mm
- 879-0350-00-04400609999_DN350_PN10: Body_Collar_Dia=102 mm; Body_Collar_Dia_2=70 mm; Body_Flange_Dia=316 mm; Body_Flange_Dia_2=350 mm; Body_Height_1=218 mm; Body_Height_2=123 mm; Body_Height_3=98 mm; Body_Height_4=138 mm; Body_Top_Dia=44 mm; Body_Top_Dia_2=37 mm; Body_With_Dia=123 mm; Body_With_Dia_1=245 mm; Body_With_Dia_2=265 mm; Bolt_support=754 mm; Bolt_support_2=377 mm; Bolt_support_Dia=30 mm  [stored 0.0984252 ft]; Bolt_support_lenght=195 mm; Bolt_support_lenght_2=205 mm; Bottom_profile=88 mm; D1=215 mm; D3=253 mm; DN=350 mm; Fillet_Length=15 mm  [stored 0.0492126 ft]; Fillet_Length_Ref=45 mm; Flange_thickness=27 mm; H=775 mm; H3_Ref=760 mm; ID=175 mm; L=980 mm; PG_Dia=117 mm; PG_Ref=145 mm; PG_depth=21 mm  [stored 0.0688976 ft]; PG_height=576 mm; PG_height_1=517 mm; PG_ref=185 mm; P_lenght=133 mm; Pilot_Dia_1=61 mm; Pilot_Dia_2=121 mm; Pilot_Dia_3=40 mm  [stored 0.131234 ft]; Pilot_Dia_4=20 mm  [stored 0.0656168 ft]; Pilot_Dia_5=13 mm; Pilot_top_1=494 mm; Profile1_Height=395 mm; Profile1_Length=68 mm; Profile1_Length_2=45 mm; Profile_Dia=15 mm  [stored 0.0492126 ft]; Profile_Dia_2=15 mm  [stored 0.0492126 ft]; Profile_Dia_3=30 mm  [stored 0.0984252 ft]; Profile_height ref=50 mm; Top_Profile=452 mm; Top_Profile_Ref=457 mm; W=630 mm; W_Ref=615 mm
- 879-0350-00-04400619999_DN350_PN10: Body_Collar_Dia=102 mm; Body_Collar_Dia_2=70 mm; Body_Flange_Dia=316 mm; Body_Flange_Dia_2=350 mm; Body_Height_1=218 mm; Body_Height_2=123 mm; Body_Height_3=98 mm; Body_Height_4=138 mm; Body_Top_Dia=44 mm; Body_Top_Dia_2=37 mm; Body_With_Dia=123 mm; Body_With_Dia_1=245 mm; Body_With_Dia_2=265 mm; Bolt_support=754 mm; Bolt_support_2=377 mm; Bolt_support_Dia=30 mm  [stored 0.0984252 ft]; Bolt_support_lenght=195 mm; Bolt_support_lenght_2=205 mm; Bottom_profile=88 mm; D1=215 mm; D3=253 mm; DN=350 mm; Fillet_Length=15 mm  [stored 0.0492126 ft]; Fillet_Length_Ref=45 mm; Flange_thickness=27 mm; H=775 mm; H3_Ref=760 mm; ID=175 mm; L=980 mm; PG_Dia=117 mm; PG_Ref=145 mm; PG_depth=21 mm  [stored 0.0688976 ft]; PG_height=576 mm; PG_height_1=517 mm; PG_ref=185 mm; P_lenght=133 mm; Pilot_Dia_1=61 mm; Pilot_Dia_2=121 mm; Pilot_Dia_3=40 mm  [stored 0.131234 ft]; Pilot_Dia_4=20 mm  [stored 0.0656168 ft]; Pilot_Dia_5=13 mm; Pilot_top_1=494 mm; Profile1_Height=395 mm; Profile1_Length=68 mm; Profile1_Length_2=45 mm; Profile_Dia=15 mm  [stored 0.0492126 ft]; Profile_Dia_2=15 mm  [stored 0.0492126 ft]; Profile_Dia_3=30 mm  [stored 0.0984252 ft]; Profile_height ref=50 mm; Top_Profile=452 mm; Top_Profile_Ref=457 mm; W=630 mm; W_Ref=615 mm
- 879-0350-00-04400629999_DN350_PN10: Body_Collar_Dia=102 mm; Body_Collar_Dia_2=70 mm; Body_Flange_Dia=316 mm; Body_Flange_Dia_2=350 mm; Body_Height_1=218 mm; Body_Height_2=123 mm; Body_Height_3=89 mm; Body_Height_4=138 mm; Body_Top_Dia=44 mm; Body_Top_Dia_2=37 mm; Body_With_Dia=123 mm; Body_With_Dia_1=245 mm; Body_With_Dia_2=265 mm; Bolt_support=754 mm; Bolt_support_2=377 mm; Bolt_support_Dia=30 mm  [stored 0.0984252 ft]; Bolt_support_lenght=195 mm; Bolt_support_lenght_2=205 mm; Bottom_profile=88 mm; D1=215 mm; D3=253 mm; DN=350 mm; Fillet_Length=15 mm  [stored 0.0492126 ft]; Fillet_Length_Ref=45 mm; Flange_thickness=27 mm; H=775 mm; H3_Ref=760 mm; ID=175 mm; L=980 mm; PG_Dia=117 mm; PG_Ref=145 mm; PG_depth=21 mm  [stored 0.0688976 ft]; PG_height=576 mm; PG_height_1=518 mm; PG_ref=185 mm; P_lenght=139 mm; Pilot_Dia_1=63 mm; Pilot_Dia_2=126 mm; Pilot_Dia_3=42 mm  [stored 0.137795 ft]; Pilot_Dia_4=21 mm  [stored 0.0688976 ft]; Pilot_Dia_5=14 mm  [stored 0.0459318 ft]; Pilot_top_1=490 mm; Profile1_Height=395 mm; Profile1_Length=68 mm; Profile1_Length_2=45 mm; Profile_Dia=15 mm  [stored 0.0492126 ft]; Profile_Dia_2=15 mm  [stored 0.0492126 ft]; Profile_Dia_3=30 mm  [stored 0.0984252 ft]; Profile_height ref=50 mm; Top_Profile=452 mm; Top_Profile_Ref=457 mm; W=630 mm; W_Ref=615 mm
- 879-0350-00-144006299A0_DN350_PN16: Body_Collar_Dia=102 mm; Body_Collar_Dia_2=70 mm; Body_Flange_Dia=316 mm; Body_Flange_Dia_2=350 mm; Body_Height_1=218 mm; Body_Height_2=123 mm; Body_Height_3=89 mm; Body_Height_4=138 mm; Body_Top_Dia=44 mm; Body_Top_Dia_2=37 mm; Body_With_Dia=123 mm; Body_With_Dia_1=245 mm; Body_With_Dia_2=265 mm; Bolt_support=754 mm; Bolt_support_2=377 mm; Bolt_support_Dia=30 mm  [stored 0.0984252 ft]; Bolt_support_lenght=195 mm; Bolt_support_lenght_2=205 mm; Bottom_profile=88 mm; D1=215 mm; D3=260 mm; DN=350 mm; Fillet_Length=15 mm  [stored 0.0492126 ft]; Fillet_Length_Ref=45 mm; Flange_thickness=27 mm; H=959 mm; H3_Ref=944 mm; ID=175 mm; L=980 mm; PG_Dia=117 mm; PG_Ref=145 mm; PG_depth=21 mm  [stored 0.0688976 ft]; PG_height=616 mm; PG_height_1=557 mm; PG_ref=185 mm; P_lenght=139 mm; Pilot_Dia_1=63 mm; Pilot_Dia_2=126 mm; Pilot_Dia_3=42 mm  [stored 0.137795 ft]; Pilot_Dia_4=21 mm  [stored 0.0688976 ft]; Pilot_Dia_5=14 mm  [stored 0.0459318 ft]; Pilot_top_1=578 mm; Profile1_Height=395 mm; Profile1_Length=70 mm; Profile1_Length_2=47 mm; Profile_Dia=15 mm  [stored 0.0492126 ft]; Profile_Dia_2=15 mm  [stored 0.0492126 ft]; Profile_Dia_3=30 mm  [stored 0.0984252 ft]; Profile_height ref=50 mm; Top_Profile=452 mm; Top_Profile_Ref=457 mm; W=630 mm; W_Ref=615 mm
- 879-0400-00-144006299A0_DN400_PN16: Body_Collar_Dia=115 mm; Body_Collar_Dia_2=79 mm; Body_Flange_Dia=355 mm; Body_Flange_Dia_2=393 mm; Body_Height_1=244 mm; Body_Height_2=138 mm; Body_Height_3=110 mm; Body_Height_4=153 mm; Body_Top_Dia=49 mm; Body_Top_Dia_2=41 mm  [stored 0.134514 ft]; Body_With_Dia=138 mm; Body_With_Dia_1=275 mm; Body_With_Dia_2=297 mm; Bolt_support=846 mm; Bolt_support_2=423 mm; Bolt_support_Dia=40 mm  [stored 0.131234 ft]; Bolt_support_lenght=220 mm; Bolt_support_lenght_2=230 mm; Bottom_profile=100 mm; D1=240 mm; D3=290 mm; DN=400 mm; Fillet_Length=20 mm  [stored 0.0656168 ft]; Fillet_Length_Ref=60 mm; Flange_thickness=28 mm  [stored 0.0918635 ft]; H=1159 mm; H3_Ref=1139 mm; ID=200 mm; L=1100 mm; PG_Dia=133 mm; PG_Ref=163 mm; PG_depth=28 mm  [stored 0.0918635 ft]; PG_height=712 mm; PG_height_1=646 mm; PG_ref=210 mm; P_lenght=152 mm; Pilot_Dia_1=69 mm; Pilot_Dia_2=138 mm; Pilot_Dia_3=46 mm; Pilot_Dia_4=23 mm  [stored 0.0754593 ft]; Pilot_Dia_5=15 mm  [stored 0.0492126 ft]; Pilot_top_1=693 mm; Profile1_Height=445 mm; Profile1_Length=78 mm; Profile1_Length_2=52 mm; Profile_Dia=20 mm  [stored 0.0656168 ft]; Profile_Dia_2=20 mm  [stored 0.0656168 ft]; Profile_Dia_3=40 mm  [stored 0.131234 ft]; Profile_height ref=55 mm; Top_Profile=508 mm; Top_Profile_Ref=513 mm; W=690 mm; W_Ref=670 mm
- 879-0450-00-144006299A0_DN450_PN16: Body_Collar_Dia=125 mm; Body_Collar_Dia_2=86 mm; Body_Flange_Dia=387 mm; Body_Flange_Dia_2=429 mm; Body_Height_1=267 mm; Body_Height_2=150 mm; Body_Height_3=120 mm; Body_Height_4=165 mm; Body_Top_Dia=54 mm; Body_Top_Dia_2=45 mm; Body_With_Dia=150 mm; Body_With_Dia_1=300 mm; Body_With_Dia_2=324 mm; Bolt_support=923 mm; Bolt_support_2=462 mm; Bolt_support_Dia=40 mm  [stored 0.131234 ft]; Bolt_support_lenght=245 mm; Bolt_support_lenght_2=255 mm; Bottom_profile=113 mm; D1=274 mm; D3=320 mm; DN=450 mm; Fillet_Length=20 mm  [stored 0.0656168 ft]; Fillet_Length_Ref=60 mm; Flange_thickness=30 mm  [stored 0.0984252 ft]; H=1220 mm; H3_Ref=1200 mm; ID=225 mm; L=1200 mm; PG_Dia=150 mm; PG_Ref=178 mm; PG_depth=28 mm  [stored 0.0918635 ft]; PG_height=758 mm; PG_height_1=683 mm; PG_ref=235 mm; P_lenght=166 mm; Pilot_Dia_1=76 mm; Pilot_Dia_2=151 mm; Pilot_Dia_3=50 mm; Pilot_Dia_4=25 mm  [stored 0.082021 ft]; Pilot_Dia_5=17 mm; Pilot_top_1=733 mm; Profile1_Height=474 mm; Profile1_Length=86 mm; Profile1_Length_2=58 mm; Profile_Dia=20 mm  [stored 0.0656168 ft]; Profile_Dia_2=20 mm  [stored 0.0656168 ft]; Profile_Dia_3=40 mm  [stored 0.131234 ft]; Profile_height ref=55 mm; Top_Profile=554 mm; Top_Profile_Ref=559 mm; W=750 mm; W_Ref=730 mm
- 879-0500-00-144006299A0_DN500_PN16: Body_Collar_Dia=130 mm; Body_Collar_Dia_2=89 mm; Body_Flange_Dia=403 mm; Body_Flange_Dia_2=446 mm; Body_Height_1=278 mm; Body_Height_2=156 mm; Body_Height_3=125 mm; Body_Height_4=171 mm; Body_Top_Dia=56 mm; Body_Top_Dia_2=47 mm; Body_With_Dia=156 mm; Body_With_Dia_1=313 mm; Body_With_Dia_2=338 mm; Bolt_support=962 mm; Bolt_support_2=481 mm; Bolt_support_Dia=50 mm; Bolt_support_lenght=270 mm; Bolt_support_lenght_2=280 mm; Bottom_profile=125 mm; D1=305 mm; D3=358 mm; DN=500 mm; Fillet_Length=25 mm  [stored 0.082021 ft]; Fillet_Length_Ref=75 mm; Flange_thickness=32 mm; H=1408 mm; H3_Ref=1383 mm; ID=250 mm; L=1250 mm; PG_Dia=167 mm; PG_Ref=185 mm; PG_depth=35 mm  [stored 0.114829 ft]; PG_height=837 mm; PG_height_1=753 mm; PG_ref=260 mm; P_lenght=183 mm; Pilot_Dia_1=83 mm; Pilot_Dia_2=166 mm; Pilot_Dia_3=55 mm; Pilot_Dia_4=28 mm  [stored 0.0918635 ft]; Pilot_Dia_5=18 mm  [stored 0.0590551 ft]; Pilot_top_1=817 mm; Profile1_Height=506 mm; Profile1_Length=97 mm; Profile1_Length_2=64 mm; Profile_Dia=25 mm  [stored 0.082021 ft]; Profile_Dia_2=25 mm  [stored 0.082021 ft]; Profile_Dia_3=50 mm; Profile_height ref=60 mm; Top_Profile=577 mm; Top_Profile_Ref=582 mm; W=825 mm; W_Ref=800 mm
- 879-0600-00-144006299A0_DN600_PN16: Body_Collar_Dia=151 mm; Body_Collar_Dia_2=104 mm; Body_Flange_Dia=468 mm; Body_Flange_Dia_2=518 mm; Body_Height_1=322 mm; Body_Height_2=181 mm; Body_Height_3=145 mm; Body_Height_4=196 mm; Body_Top_Dia=65 mm; Body_Top_Dia_2=54 mm; Body_With_Dia=181 mm; Body_With_Dia_1=363 mm; Body_With_Dia_2=392 mm; Bolt_support=1115 mm; Bolt_support_2=558 mm; Bolt_support_Dia=60 mm; Bolt_support_lenght=320 mm; Bolt_support_lenght_2=330 mm; Bottom_profile=150 mm; D1=360 mm; D3=420 mm; DN=600 mm; Fillet_Length=30 mm  [stored 0.0984252 ft]; Fillet_Length_Ref=90 mm; Flange_thickness=36 mm  [stored 0.11811 ft]; H=1518 mm; H3_Ref=1488 mm; ID=300 mm; L=1450 mm; PG_Dia=200 mm; PG_Ref=215 mm; PG_depth=42 mm  [stored 0.137795 ft]; PG_height=941 mm; PG_height_1=841 mm; PG_ref=310 mm; P_lenght=216 mm; Pilot_Dia_1=98 mm; Pilot_Dia_2=196 mm; Pilot_Dia_3=65 mm; Pilot_Dia_4=33 mm; Pilot_Dia_5=22 mm  [stored 0.0721785 ft]; Pilot_top_1=886 mm; Profile1_Height=581 mm; Profile1_Length=114 mm; Profile1_Length_2=76 mm; Profile_Dia=30 mm  [stored 0.0984252 ft]; Profile_Dia_2=30 mm  [stored 0.0984252 ft]; Profile_Dia_3=60 mm; Profile_height ref=65 mm; Top_Profile=669 mm; Top_Profile_Ref=674 mm; W=950 mm; W_Ref=920 mm

note: [stored X ft] marks values corroborated as IEEE doubles in the binary element streams (Revit-internal decimal feet)

## geometry (parser evidence)
native form markers: Sweep x3
no freeform markers — native parametric forms only
